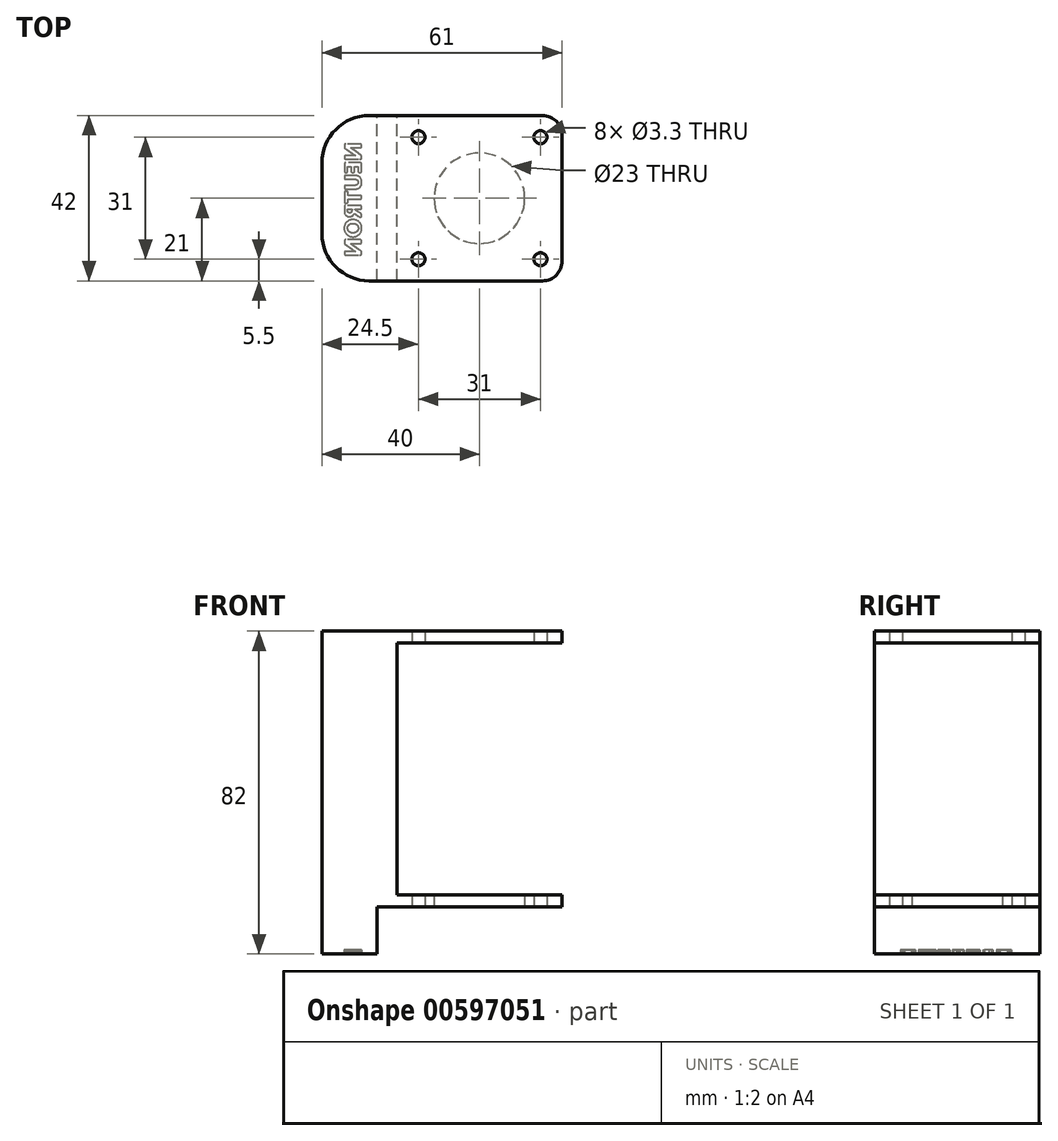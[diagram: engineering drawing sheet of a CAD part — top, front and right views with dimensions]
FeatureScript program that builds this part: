
annotation { "Feature Type Name" : "Feature", "Feature Type Description" : "" }
export const myFeature = defineFeature(function(context is Context, id is Id, definition is map)
    precondition{}
    {
        {
            var Q0;
            Q0=qCreatedBy(makeId("Top.planeOp"),FACE);
            var sketch = newSketch(context, id + "F0", { "sketchPlane" : qUnion([Q0])});
            skLineSegment(sketch, "E0.bottom", {"start": v(21, -21) * mm, "end": v(-21, -21) * mm});
            skLineSegment(sketch, "E0.top", {"start": v(21, 21) * mm, "end": v(-21, 21) * mm});
            skLineSegment(sketch, "E0.left", {"start": v(21, -21) * mm, "end": v(21, 21) * mm});
            skLineSegment(sketch, "E0.right", {"start": v(-21, -21) * mm, "end": v(-21, 21) * mm});
            skPoint(sketch, "E0.middle", {"position": v(0, 0) * mm});
            skSolve(sketch);
        }
        {
            var Q0;
            Q0=makeQuery(id+"F0.imprint","IMPRINT",FACE,{"disambiguationData":[TD([[makeQuery(id+"F0.imprint","IMPRINT",EDGE,{"derivedFrom":sQuery(id+"F0.wireOp",EDGE,"E0.bottom")}),-1.0]])]});
            extrude(context, id + "F1", {"entities" : qUnion([Q0]), "depth" : 3 * mm});
        }
        {
            var Q0;
            Q0=makeQuery(id+"F1.opExtrude","CAP_FACE",FACE,{"disambiguationData":[OSD([sQuery(id+"F0.wireOp",EDGE,"E0.bottom"),sQuery(id+"F0.wireOp",EDGE,"E0.top"),sQuery(id+"F0.wireOp",EDGE,"E0.left"),sQuery(id+"F0.wireOp",EDGE,"E0.right")])],"isStart":true});
            var sketch = newSketch(context, id + "F2", { "sketchPlane" : qUnion([Q0])});
            skLineSegment(sketch, "E1.bottom", {"start": v(-15.5, 15.5) * mm, "end": v(15.5, 15.5) * mm});
            skLineSegment(sketch, "E1.top", {"start": v(-15.5, -15.5) * mm, "end": v(15.5, -15.5) * mm});
            skLineSegment(sketch, "E1.left", {"start": v(-15.5, 15.5) * mm, "end": v(-15.5, -15.5) * mm});
            skLineSegment(sketch, "E1.right", {"start": v(15.5, 15.5) * mm, "end": v(15.5, -15.5) * mm});
            skPoint(sketch, "E1.middle", {"position": v(0, 0) * mm});
            skCircle(sketch, "E2", {"center": v(0, 0) * mm, "radius": 11.5 * mm});
            skSolve(sketch);
        }
        {
            var Q0;
            Q0=makeQuery(id+"F2.imprint","IMPRINT",FACE,{"disambiguationData":[TD([[makeQuery(id+"F2.imprint","IMPRINT",EDGE,{"derivedFrom":sQuery(id+"F2.wireOp",EDGE,"E2")}),1.0]])]});
            extrude(context, id + "F3", {"entities" : qUnion([Q0]), "operationType" : NewBodyOperationType.REMOVE, "oppositeDirection" : true, "depth" : 25 * mm});
        }
        {
            var Q0;
            Q0=makeQuery(id+"F1.opExtrude","SWEPT_FACE",FACE,{"disambiguationData":[OSD([sQuery(id+"F0.wireOp",EDGE,"E0.right")])]});
            var sketch = newSketch(context, id + "F4", { "sketchPlane" : qUnion([Q0])});
            skLineSegment(sketch, "E3.bottom", {"start": v(21, 0) * mm, "end": v(-21, 0) * mm});
            skLineSegment(sketch, "E3.top", {"start": v(21, 70) * mm, "end": v(-21, 70) * mm});
            skLineSegment(sketch, "E3.left", {"start": v(21, 0) * mm, "end": v(21, 70) * mm});
            skLineSegment(sketch, "E3.right", {"start": v(-21, 0) * mm, "end": v(-21, 70) * mm});
            skSolve(sketch);
        }
        {
            var Q0;
            {var subQ0=sQuery(id+"F4.wireOp",EDGE,"E3.bottom");Q0=makeQuery(id+"F4.imprint","IMPRINT",FACE,{"disambiguationData":[TD([[makeQuery(id+"F4.imprint","IMPRINT",EDGE,{"derivedFrom":subQ0}),-1.0]])]});}
            var Q1;
            {var subQ0=sQuery(id+"F4.wireOp",EDGE,"E3.top");Q1=makeQuery(id+"F4.imprint","IMPRINT",FACE,{"disambiguationData":[TD([[makeQuery(id+"F4.imprint","IMPRINT",EDGE,{"derivedFrom":subQ0}),1.0]])]});}
            extrude(context, id + "F5", {"entities" : qUnion([Q0, Q1]), "operationType" : NewBodyOperationType.ADD, "depth" : 19 * mm});
        }
        {
            var Q0;
            Q0=makeQuery(id+"F5.opExtrude","CAP_FACE",FACE,{"disambiguationData":[OSD([sQuery(id+"F4.wireOp",EDGE,"E3.bottom"),sQuery(id+"F4.wireOp",EDGE,"E3.top"),sQuery(id+"F4.wireOp",EDGE,"E3.left"),sQuery(id+"F4.wireOp",EDGE,"E3.right")])],"isStart":true});
            var sketch = newSketch(context, id + "F6", { "sketchPlane" : qUnion([Q0])});
            skLineSegment(sketch, "E4.bottom", {"start": v(21, 70) * mm, "end": v(-21, 70) * mm});
            skLineSegment(sketch, "E4.top", {"start": v(21, 67) * mm, "end": v(-21, 67) * mm});
            skLineSegment(sketch, "E4.left", {"start": v(21, 70) * mm, "end": v(21, 67) * mm});
            skLineSegment(sketch, "E4.right", {"start": v(-21, 70) * mm, "end": v(-21, 67) * mm});
            skSolve(sketch);
        }
        {
            var Q0;
            Q0=qSketchRegion(id+"F6",true);
            extrude(context, id + "F7", {"entities" : qUnion([Q0]), "operationType" : NewBodyOperationType.ADD, "depth" : 42 * mm});
        }
        {
            var Q0;
            Q0=makeQuery(id+"F1.opExtrude","SWEPT_EDGE",EDGE,{"disambiguationData":[OSD([sQuery(id+"F0.wireOp",EDGE,"E0.top"),sQuery(id+"F0.wireOp",EDGE,"E0.left")])]});
            var Q1;
            Q1=makeQuery(id+"F1.opExtrude","SWEPT_EDGE",EDGE,{"disambiguationData":[OSD([sQuery(id+"F0.wireOp",EDGE,"E0.bottom"),sQuery(id+"F0.wireOp",EDGE,"E0.left")])]});
            var Q2;
            Q2=makeQuery(id+"F7.opExtrude","CAP_EDGE",EDGE,{"disambiguationData":[OSD([sQuery(id+"F6.wireOp",EDGE,"E4.right")])],"isStart":false});
            var Q3;
            Q3=makeQuery(id+"F7.opExtrude","CAP_EDGE",EDGE,{"disambiguationData":[OSD([sQuery(id+"F6.wireOp",EDGE,"E4.left")])],"isStart":false});
            fillet(context, id + "F8", {"entities" : qUnion([Q0, Q1, Q2, Q3]), "radius" : 5 * mm, "tangentPropagation" : true, "allowEdgeOverflow" : false});
        }
        {
            var Q0;
            Q0=sQuery(id+"F2.wireOp",VERTEX,"E1.left.end");
            var Q1;
            Q1=sQuery(id+"F2.wireOp",VERTEX,"E1.right.end");
            var Q2;
            Q2=sQuery(id+"F2.wireOp",VERTEX,"E1.right.start");
            var Q3;
            Q3=sQuery(id+"F2.wireOp",VERTEX,"E1.left.start");
            var Q4;
            Q4=makeQuery(id+"F1.opExtrude","SWEPT_BODY",BODY,{"disambiguationData":[OSD([sQuery(id+"F0.wireOp",EDGE,"E0.bottom"),sQuery(id+"F0.wireOp",EDGE,"E0.top"),sQuery(id+"F0.wireOp",EDGE,"E0.left"),sQuery(id+"F0.wireOp",EDGE,"E0.right")])]});
            hole(context, id + "F9", {"style" : HoleStyle.SIMPLE, "endStyle" : HoleEndStyle.THROUGH, "standardTappedOrClearance" : lookupTablePath({ "standard" : "ISO", "fit" : "Normal", "size" : "M3", "type" : "Clearance" }), "standardBlindInLast" : lookupTablePath({ "fit" : "Standard", "standard" : "ISO", "size" : "M3", "type" : "Clearance" }), "holeDiameter" : 3.3 * mm, "tappedDepth" : 12 * mm, "tapClearance" : 3, "locations" : qUnion([Q0, Q1, Q2, Q3]), "scope" : qUnion([Q4])});
        }
        {
            var Q0;
            Q0=makeQuery(id+"F5.opExtrude","CAP_EDGE",EDGE,{"disambiguationData":[OSD([sQuery(id+"F4.wireOp",EDGE,"E3.left")])],"isStart":false});
            var Q1;
            Q1=makeQuery(id+"F5.opExtrude","CAP_EDGE",EDGE,{"disambiguationData":[OSD([sQuery(id+"F4.wireOp",EDGE,"E3.right")])],"isStart":false});
            fillet(context, id + "F10", {"entities" : qUnion([Q0, Q1]), "radius" : 12 * mm, "tangentPropagation" : true, "allowEdgeOverflow" : false});
        }
        {
            var Q0;
            Q0=makeQuery(id+"F5.boolean.opBoolean","MERGE",FACE,{"derivedFrom":[makeQuery(id+"F1.opExtrude","CAP_FACE",FACE,{"disambiguationData":[OSD([sQuery(id+"F0.wireOp",EDGE,"E0.bottom"),sQuery(id+"F0.wireOp",EDGE,"E0.top"),sQuery(id+"F0.wireOp",EDGE,"E0.left"),sQuery(id+"F0.wireOp",EDGE,"E0.right")])],"isStart":true}),makeQuery(id+"F5.opExtrude","SWEPT_FACE",FACE,{"disambiguationData":[OSD([sQuery(id+"F4.wireOp",EDGE,"E3.bottom")])]})]});
            var sketch = newSketch(context, id + "F11", { "sketchPlane" : qUnion([Q0])});
            skLineSegment(sketch, "E5", {"start": v(-26, 21) * mm, "end": v(-26, -21) * mm});
            skSolve(sketch);
        }
        {
            var Q0;
            Q0=qSketchRegion(id+"F11",true);
            var Q1;
            Q1=makeQuery(id+"F11.imprint","IMPRINT",FACE,{"disambiguationData":[TD([[makeQuery(id+"F11.imprint","IMPRINT",EDGE,{"derivedFrom":sQuery(id+"F11.wireOp",EDGE,"xwHfM6YB-dKn8-eSAS-4Oin-q8f2QlFwRjm7")}),1.0]])]});
            var Q2;
            {var subQ6=sQuery(id+"F11.wireOp",EDGE,"E5");Q2=makeQuery(id+"F11.imprint","IMPRINT",FACE,{"disambiguationData":[TD([[makeQuery(id+"F11.imprint","IMPRINT",EDGE,{"derivedFrom":subQ6}),-1.0]])]});}
            extrude(context, id + "F12", {"entities" : qUnion([Q0, Q1, Q2]), "operationType" : NewBodyOperationType.ADD, "depth" : 12 * mm});
        }
        {
            var Q0;
            Q0=makeQuery(id+"F12.opExtrude","CAP_FACE",FACE,{"disambiguationData":[OSD([sQuery(id+"F0.wireOp",EDGE,"E0.bottom"),sQuery(id+"F0.wireOp",EDGE,"E0.top"),sQuery(id+"F0.wireOp",EDGE,"E0.left"),sQuery(id+"F0.wireOp",EDGE,"E0.right"),sQuery(id+"F4.wireOp",EDGE,"E3.bottom"),sQuery(id+"F4.wireOp",EDGE,"E3.left"),sQuery(id+"F4.wireOp",EDGE,"E3.right"),sQuery(id+"F11.wireOp",EDGE,"xwHfM6YB-dKn8-eSAS-4Oin-q8f2QlFwRjm7")])],"isStart":false});
            var sketch = newSketch(context, id + "F13", { "sketchPlane" : qUnion([Q0])});
            skLineSegment(sketch, "E6", {"start": v(-34.33, -10.53) * mm, "end": v(-34.33, -10.5) * mm});
            skLineSegment(sketch, "E7", {"start": v(-34.33, -10.5) * mm, "end": v(-34.33, -10.44) * mm});
            skLineSegment(sketch, "E8", {"start": v(-34.33, -10.44) * mm, "end": v(-34.33, -10.36) * mm});
            skLineSegment(sketch, "E9", {"start": v(-34.33, -10.36) * mm, "end": v(-34.33, -10.28) * mm});
            skLineSegment(sketch, "E10", {"start": v(-34.33, -10.28) * mm, "end": v(-34.33, -10.23) * mm});
            skLineSegment(sketch, "E11", {"start": v(-34.33, -10.23) * mm, "end": v(-34.33, -10.18) * mm});
            skLineSegment(sketch, "E12", {"start": v(-34.33, -10.18) * mm, "end": v(-34.3, -10.1) * mm});
            skLineSegment(sketch, "E13", {"start": v(-34.3, -10.1) * mm, "end": v(-34.26, -10.02) * mm});
            skLineSegment(sketch, "E14", {"start": v(-34.26, -10.02) * mm, "end": v(-34.2, -9.97) * mm});
            skLineSegment(sketch, "E15", {"start": v(-34.2, -9.97) * mm, "end": v(-34.12, -9.93) * mm});
            skLineSegment(sketch, "E16", {"start": v(-34.12, -9.93) * mm, "end": v(-34.03, -9.91) * mm});
            skLineSegment(sketch, "E17", {"start": v(-34.03, -9.91) * mm, "end": v(-33.76, -9.91) * mm});
            skLineSegment(sketch, "E18", {"start": v(-33.76, -9.91) * mm, "end": v(-33.01, -9.91) * mm});
            skLineSegment(sketch, "E19", {"start": v(-33.01, -9.91) * mm, "end": v(-32.03, -9.91) * mm});
            skLineSegment(sketch, "E20", {"start": v(-32.03, -9.91) * mm, "end": v(-31.07, -9.91) * mm});
            skLineSegment(sketch, "E21", {"start": v(-31.07, -9.91) * mm, "end": v(-30.41, -9.91) * mm});
            skLineSegment(sketch, "E22", {"start": v(-30.41, -9.91) * mm, "end": v(-30.23, -9.91) * mm});
            skLineSegment(sketch, "E23", {"start": v(-30.23, -9.91) * mm, "end": v(-30.15, -9.93) * mm});
            skLineSegment(sketch, "E24", {"start": v(-30.15, -9.93) * mm, "end": v(-30.07, -9.98) * mm});
            skLineSegment(sketch, "E25", {"start": v(-30.07, -9.98) * mm, "end": v(-30.01, -10.04) * mm});
            skLineSegment(sketch, "E26", {"start": v(-30.01, -10.04) * mm, "end": v(-29.97, -10.11) * mm});
            skLineSegment(sketch, "E27", {"start": v(-29.97, -10.11) * mm, "end": v(-29.95, -10.2) * mm});
            skLineSegment(sketch, "E28", {"start": v(-29.95, -10.2) * mm, "end": v(-29.95, -10.25) * mm});
            skLineSegment(sketch, "E29", {"start": v(-29.95, -10.25) * mm, "end": v(-29.95, -10.33) * mm});
            skLineSegment(sketch, "E30", {"start": v(-29.95, -10.33) * mm, "end": v(-29.95, -10.45) * mm});
            skLineSegment(sketch, "E31", {"start": v(-29.95, -10.45) * mm, "end": v(-29.95, -10.56) * mm});
            skLineSegment(sketch, "E32", {"start": v(-29.95, -10.56) * mm, "end": v(-29.95, -10.65) * mm});
            skLineSegment(sketch, "E33", {"start": v(-29.95, -10.65) * mm, "end": v(-29.95, -10.68) * mm});
            skLineSegment(sketch, "E34", {"start": v(-29.95, -10.68) * mm, "end": v(-29.96, -10.74) * mm});
            skLineSegment(sketch, "E35", {"start": v(-29.96, -10.74) * mm, "end": v(-29.98, -10.79) * mm});
            skLineSegment(sketch, "E36", {"start": v(-29.98, -10.79) * mm, "end": v(-30, -10.83) * mm});
            skLineSegment(sketch, "E37", {"start": v(-30, -10.83) * mm, "end": v(-30.03, -10.88) * mm});
            skLineSegment(sketch, "E38", {"start": v(-30.03, -10.88) * mm, "end": v(-30.07, -10.91) * mm});
            skLineSegment(sketch, "E39", {"start": v(-30.07, -10.91) * mm, "end": v(-30.2, -11) * mm});
            skLineSegment(sketch, "E40", {"start": v(-30.2, -11) * mm, "end": v(-30.67, -11.34) * mm});
            skLineSegment(sketch, "E41", {"start": v(-30.67, -11.34) * mm, "end": v(-31.35, -11.82) * mm});
            skLineSegment(sketch, "E42", {"start": v(-31.35, -11.82) * mm, "end": v(-32.06, -12.32) * mm});
            skLineSegment(sketch, "E43", {"start": v(-32.06, -12.32) * mm, "end": v(-32.6, -12.7) * mm});
            skLineSegment(sketch, "E44", {"start": v(-32.6, -12.7) * mm, "end": v(-32.78, -12.83) * mm});
            skLineSegment(sketch, "E45", {"start": v(-32.78, -12.83) * mm, "end": v(-32.52, -12.83) * mm});
            skLineSegment(sketch, "E46", {"start": v(-32.52, -12.83) * mm, "end": v(-31.97, -12.83) * mm});
            skLineSegment(sketch, "E47", {"start": v(-31.97, -12.83) * mm, "end": v(-31.3, -12.83) * mm});
            skLineSegment(sketch, "E48", {"start": v(-31.3, -12.83) * mm, "end": v(-30.68, -12.83) * mm});
            skLineSegment(sketch, "E49", {"start": v(-30.68, -12.83) * mm, "end": v(-30.3, -12.83) * mm});
            skLineSegment(sketch, "E50", {"start": v(-30.3, -12.83) * mm, "end": v(-30.21, -12.84) * mm});
            skLineSegment(sketch, "E51", {"start": v(-30.21, -12.84) * mm, "end": v(-30.13, -12.86) * mm});
            skLineSegment(sketch, "E52", {"start": v(-30.13, -12.86) * mm, "end": v(-30.06, -12.9) * mm});
            skLineSegment(sketch, "E53", {"start": v(-30.06, -12.9) * mm, "end": v(-30, -12.97) * mm});
            skLineSegment(sketch, "E54", {"start": v(-30, -12.97) * mm, "end": v(-29.97, -13.05) * mm});
            skLineSegment(sketch, "E55", {"start": v(-29.97, -13.05) * mm, "end": v(-29.95, -13.14) * mm});
            skLineSegment(sketch, "E56", {"start": v(-29.95, -13.14) * mm, "end": v(-29.95, -13.17) * mm});
            skLineSegment(sketch, "E57", {"start": v(-29.95, -13.17) * mm, "end": v(-29.95, -13.24) * mm});
            skLineSegment(sketch, "E58", {"start": v(-29.95, -13.24) * mm, "end": v(-29.95, -13.32) * mm});
            skLineSegment(sketch, "E59", {"start": v(-29.95, -13.32) * mm, "end": v(-29.95, -13.4) * mm});
            skLineSegment(sketch, "E60", {"start": v(-29.95, -13.4) * mm, "end": v(-29.95, -13.46) * mm});
            skLineSegment(sketch, "E61", {"start": v(-29.95, -13.46) * mm, "end": v(-29.96, -13.5) * mm});
            skLineSegment(sketch, "E62", {"start": v(-29.96, -13.5) * mm, "end": v(-29.98, -13.6) * mm});
            skLineSegment(sketch, "E63", {"start": v(-29.98, -13.6) * mm, "end": v(-30.02, -13.66) * mm});
            skLineSegment(sketch, "E64", {"start": v(-30.02, -13.66) * mm, "end": v(-30.09, -13.72) * mm});
            skLineSegment(sketch, "E65", {"start": v(-30.09, -13.72) * mm, "end": v(-30.16, -13.76) * mm});
            skLineSegment(sketch, "E66", {"start": v(-30.16, -13.76) * mm, "end": v(-30.25, -13.78) * mm});
            skLineSegment(sketch, "E67", {"start": v(-30.25, -13.78) * mm, "end": v(-30.52, -13.78) * mm});
            skLineSegment(sketch, "E68", {"start": v(-30.52, -13.78) * mm, "end": v(-31.27, -13.78) * mm});
            skLineSegment(sketch, "E69", {"start": v(-31.27, -13.78) * mm, "end": v(-32.25, -13.78) * mm});
            skLineSegment(sketch, "E70", {"start": v(-32.25, -13.78) * mm, "end": v(-33.2, -13.78) * mm});
            skLineSegment(sketch, "E71", {"start": v(-33.2, -13.78) * mm, "end": v(-33.87, -13.78) * mm});
            skLineSegment(sketch, "E72", {"start": v(-33.87, -13.78) * mm, "end": v(-34.05, -13.77) * mm});
            skLineSegment(sketch, "E73", {"start": v(-34.05, -13.77) * mm, "end": v(-34.14, -13.75) * mm});
            skLineSegment(sketch, "E74", {"start": v(-34.14, -13.75) * mm, "end": v(-34.21, -13.71) * mm});
            skLineSegment(sketch, "E75", {"start": v(-34.21, -13.71) * mm, "end": v(-34.27, -13.65) * mm});
            skLineSegment(sketch, "E76", {"start": v(-34.27, -13.65) * mm, "end": v(-34.31, -13.57) * mm});
            skLineSegment(sketch, "E77", {"start": v(-34.31, -13.57) * mm, "end": v(-34.33, -13.49) * mm});
            skLineSegment(sketch, "E78", {"start": v(-34.33, -13.49) * mm, "end": v(-34.33, -13.44) * mm});
            skLineSegment(sketch, "E79", {"start": v(-34.33, -13.44) * mm, "end": v(-34.33, -13.35) * mm});
            skLineSegment(sketch, "E80", {"start": v(-34.33, -13.35) * mm, "end": v(-34.33, -13.23) * mm});
            skLineSegment(sketch, "E81", {"start": v(-34.33, -13.23) * mm, "end": v(-34.33, -13.11) * mm});
            skLineSegment(sketch, "E82", {"start": v(-34.33, -13.11) * mm, "end": v(-34.33, -13.03) * mm});
            skLineSegment(sketch, "E83", {"start": v(-34.33, -13.03) * mm, "end": v(-34.33, -12.99) * mm});
            skLineSegment(sketch, "E84", {"start": v(-34.33, -12.99) * mm, "end": v(-34.32, -12.94) * mm});
            skLineSegment(sketch, "E85", {"start": v(-34.32, -12.94) * mm, "end": v(-34.3, -12.89) * mm});
            skLineSegment(sketch, "E86", {"start": v(-34.3, -12.89) * mm, "end": v(-34.28, -12.84) * mm});
            skLineSegment(sketch, "E87", {"start": v(-34.28, -12.84) * mm, "end": v(-34.25, -12.8) * mm});
            skLineSegment(sketch, "E88", {"start": v(-34.25, -12.8) * mm, "end": v(-34.21, -12.76) * mm});
            skLineSegment(sketch, "E89", {"start": v(-34.21, -12.76) * mm, "end": v(-34.1, -12.67) * mm});
            skLineSegment(sketch, "E90", {"start": v(-34.1, -12.67) * mm, "end": v(-33.62, -12.34) * mm});
            skLineSegment(sketch, "E91", {"start": v(-33.62, -12.34) * mm, "end": v(-32.94, -11.85) * mm});
            skLineSegment(sketch, "E92", {"start": v(-32.94, -11.85) * mm, "end": v(-32.24, -11.35) * mm});
            skLineSegment(sketch, "E93", {"start": v(-32.24, -11.35) * mm, "end": v(-31.7, -10.97) * mm});
            skLineSegment(sketch, "E94", {"start": v(-31.7, -10.97) * mm, "end": v(-31.52, -10.84) * mm});
            skLineSegment(sketch, "E95", {"start": v(-31.52, -10.84) * mm, "end": v(-31.78, -10.84) * mm});
            skLineSegment(sketch, "E96", {"start": v(-31.78, -10.84) * mm, "end": v(-32.33, -10.84) * mm});
            skLineSegment(sketch, "E97", {"start": v(-32.33, -10.84) * mm, "end": v(-33, -10.84) * mm});
            skLineSegment(sketch, "E98", {"start": v(-33, -10.84) * mm, "end": v(-33.6, -10.84) * mm});
            skLineSegment(sketch, "E99", {"start": v(-33.6, -10.84) * mm, "end": v(-33.97, -10.84) * mm});
            skLineSegment(sketch, "E100", {"start": v(-33.97, -10.84) * mm, "end": v(-34.07, -10.83) * mm});
            skLineSegment(sketch, "E101", {"start": v(-34.07, -10.83) * mm, "end": v(-34.15, -10.8) * mm});
            skLineSegment(sketch, "E102", {"start": v(-34.15, -10.8) * mm, "end": v(-34.22, -10.76) * mm});
            skLineSegment(sketch, "E103", {"start": v(-34.22, -10.76) * mm, "end": v(-34.28, -10.7) * mm});
            skLineSegment(sketch, "E104", {"start": v(-34.28, -10.7) * mm, "end": v(-34.32, -10.62) * mm});
            skLineSegment(sketch, "E105", {"start": v(-34.32, -10.62) * mm, "end": v(-34.33, -10.53) * mm});
            skLineSegment(sketch, "E106", {"start": v(-34.33, -8.72) * mm, "end": v(-34.33, -8.52) * mm});
            skLineSegment(sketch, "E107", {"start": v(-34.33, -8.52) * mm, "end": v(-34.33, -8.07) * mm});
            skLineSegment(sketch, "E108", {"start": v(-34.33, -8.07) * mm, "end": v(-34.33, -7.52) * mm});
            skLineSegment(sketch, "E109", {"start": v(-34.33, -7.52) * mm, "end": v(-34.33, -7.06) * mm});
            skLineSegment(sketch, "E110", {"start": v(-34.33, -7.06) * mm, "end": v(-34.33, -6.87) * mm});
            skLineSegment(sketch, "E111", {"start": v(-34.33, -6.87) * mm, "end": v(-34.31, -6.77) * mm});
            skLineSegment(sketch, "E112", {"start": v(-34.31, -6.77) * mm, "end": v(-34.27, -6.69) * mm});
            skLineSegment(sketch, "E113", {"start": v(-34.27, -6.69) * mm, "end": v(-34.2, -6.62) * mm});
            skLineSegment(sketch, "E114", {"start": v(-34.2, -6.62) * mm, "end": v(-34.12, -6.58) * mm});
            skLineSegment(sketch, "E115", {"start": v(-34.12, -6.58) * mm, "end": v(-34.02, -6.56) * mm});
            skLineSegment(sketch, "E116", {"start": v(-34.02, -6.56) * mm, "end": v(-34, -6.56) * mm});
            skLineSegment(sketch, "E117", {"start": v(-34, -6.56) * mm, "end": v(-33.93, -6.56) * mm});
            skLineSegment(sketch, "E118", {"start": v(-33.93, -6.56) * mm, "end": v(-33.86, -6.56) * mm});
            skLineSegment(sketch, "E119", {"start": v(-33.86, -6.56) * mm, "end": v(-33.8, -6.56) * mm});
            skLineSegment(sketch, "E120", {"start": v(-33.8, -6.56) * mm, "end": v(-33.77, -6.56) * mm});
            skLineSegment(sketch, "E121", {"start": v(-33.77, -6.56) * mm, "end": v(-33.67, -6.58) * mm});
            skLineSegment(sketch, "E122", {"start": v(-33.67, -6.58) * mm, "end": v(-33.59, -6.62) * mm});
            skLineSegment(sketch, "E123", {"start": v(-33.59, -6.62) * mm, "end": v(-33.52, -6.69) * mm});
            skLineSegment(sketch, "E124", {"start": v(-33.52, -6.69) * mm, "end": v(-33.48, -6.77) * mm});
            skLineSegment(sketch, "E125", {"start": v(-33.48, -6.77) * mm, "end": v(-33.46, -6.87) * mm});
            skLineSegment(sketch, "E126", {"start": v(-33.46, -6.87) * mm, "end": v(-33.46, -7) * mm});
            skLineSegment(sketch, "E127", {"start": v(-33.46, -7) * mm, "end": v(-33.46, -7.3) * mm});
            skLineSegment(sketch, "E128", {"start": v(-33.46, -7.3) * mm, "end": v(-33.46, -7.66) * mm});
            skLineSegment(sketch, "E129", {"start": v(-33.46, -7.66) * mm, "end": v(-33.46, -7.96) * mm});
            skLineSegment(sketch, "E130", {"start": v(-33.46, -7.96) * mm, "end": v(-33.46, -8.08) * mm});
            skLineSegment(sketch, "E131", {"start": v(-33.46, -8.08) * mm, "end": v(-33.37, -8.08) * mm});
            skLineSegment(sketch, "E132", {"start": v(-33.37, -8.08) * mm, "end": v(-33.15, -8.08) * mm});
            skLineSegment(sketch, "E133", {"start": v(-33.15, -8.08) * mm, "end": v(-32.9, -8.08) * mm});
            skLineSegment(sketch, "E134", {"start": v(-32.9, -8.08) * mm, "end": v(-32.67, -8.08) * mm});
            skLineSegment(sketch, "E135", {"start": v(-32.67, -8.08) * mm, "end": v(-32.58, -8.08) * mm});
            skLineSegment(sketch, "E136", {"start": v(-32.58, -8.08) * mm, "end": v(-32.58, -7.96) * mm});
            skLineSegment(sketch, "E137", {"start": v(-32.58, -7.96) * mm, "end": v(-32.58, -7.66) * mm});
            skLineSegment(sketch, "E138", {"start": v(-32.58, -7.66) * mm, "end": v(-32.58, -7.3) * mm});
            skLineSegment(sketch, "E139", {"start": v(-32.58, -7.3) * mm, "end": v(-32.58, -7) * mm});
            skLineSegment(sketch, "E140", {"start": v(-32.58, -7) * mm, "end": v(-32.58, -6.87) * mm});
            skLineSegment(sketch, "E141", {"start": v(-32.58, -6.87) * mm, "end": v(-32.56, -6.77) * mm});
            skLineSegment(sketch, "E142", {"start": v(-32.56, -6.77) * mm, "end": v(-32.52, -6.69) * mm});
            skLineSegment(sketch, "E143", {"start": v(-32.52, -6.69) * mm, "end": v(-32.45, -6.62) * mm});
            skLineSegment(sketch, "E144", {"start": v(-32.45, -6.62) * mm, "end": v(-32.37, -6.58) * mm});
            skLineSegment(sketch, "E145", {"start": v(-32.37, -6.58) * mm, "end": v(-32.27, -6.56) * mm});
            skLineSegment(sketch, "E146", {"start": v(-32.27, -6.56) * mm, "end": v(-32.25, -6.56) * mm});
            skLineSegment(sketch, "E147", {"start": v(-32.25, -6.56) * mm, "end": v(-32.19, -6.56) * mm});
            skLineSegment(sketch, "E148", {"start": v(-32.19, -6.56) * mm, "end": v(-32.12, -6.56) * mm});
            skLineSegment(sketch, "E149", {"start": v(-32.12, -6.56) * mm, "end": v(-32.06, -6.56) * mm});
            skLineSegment(sketch, "E150", {"start": v(-32.06, -6.56) * mm, "end": v(-32.04, -6.56) * mm});
            skLineSegment(sketch, "E151", {"start": v(-32.04, -6.56) * mm, "end": v(-31.94, -6.58) * mm});
            skLineSegment(sketch, "E152", {"start": v(-31.94, -6.58) * mm, "end": v(-31.85, -6.62) * mm});
            skLineSegment(sketch, "E153", {"start": v(-31.85, -6.62) * mm, "end": v(-31.79, -6.69) * mm});
            skLineSegment(sketch, "E154", {"start": v(-31.79, -6.69) * mm, "end": v(-31.74, -6.77) * mm});
            skLineSegment(sketch, "E155", {"start": v(-31.74, -6.77) * mm, "end": v(-31.73, -6.87) * mm});
            skLineSegment(sketch, "E156", {"start": v(-31.73, -6.87) * mm, "end": v(-31.73, -7) * mm});
            skLineSegment(sketch, "E157", {"start": v(-31.73, -7) * mm, "end": v(-31.73, -7.3) * mm});
            skLineSegment(sketch, "E158", {"start": v(-31.73, -7.3) * mm, "end": v(-31.73, -7.66) * mm});
            skLineSegment(sketch, "E159", {"start": v(-31.73, -7.66) * mm, "end": v(-31.73, -7.96) * mm});
            skLineSegment(sketch, "E160", {"start": v(-31.73, -7.96) * mm, "end": v(-31.73, -8.08) * mm});
            skLineSegment(sketch, "E161", {"start": v(-31.73, -8.08) * mm, "end": v(-31.63, -8.08) * mm});
            skLineSegment(sketch, "E162", {"start": v(-31.63, -8.08) * mm, "end": v(-31.4, -8.08) * mm});
            skLineSegment(sketch, "E163", {"start": v(-31.4, -8.08) * mm, "end": v(-31.14, -8.08) * mm});
            skLineSegment(sketch, "E164", {"start": v(-31.14, -8.08) * mm, "end": v(-30.91, -8.08) * mm});
            skLineSegment(sketch, "E165", {"start": v(-30.91, -8.08) * mm, "end": v(-30.82, -8.08) * mm});
            skLineSegment(sketch, "E166", {"start": v(-30.82, -8.08) * mm, "end": v(-30.82, -7.96) * mm});
            skLineSegment(sketch, "E167", {"start": v(-30.82, -7.96) * mm, "end": v(-30.82, -7.66) * mm});
            skLineSegment(sketch, "E168", {"start": v(-30.82, -7.66) * mm, "end": v(-30.82, -7.3) * mm});
            skLineSegment(sketch, "E169", {"start": v(-30.82, -7.3) * mm, "end": v(-30.82, -7) * mm});
            skLineSegment(sketch, "E170", {"start": v(-30.82, -7) * mm, "end": v(-30.82, -6.87) * mm});
            skLineSegment(sketch, "E171", {"start": v(-30.82, -6.87) * mm, "end": v(-30.8, -6.77) * mm});
            skLineSegment(sketch, "E172", {"start": v(-30.8, -6.77) * mm, "end": v(-30.76, -6.69) * mm});
            skLineSegment(sketch, "E173", {"start": v(-30.76, -6.69) * mm, "end": v(-30.7, -6.62) * mm});
            skLineSegment(sketch, "E174", {"start": v(-30.7, -6.62) * mm, "end": v(-30.6, -6.58) * mm});
            skLineSegment(sketch, "E175", {"start": v(-30.6, -6.58) * mm, "end": v(-30.51, -6.56) * mm});
            skLineSegment(sketch, "E176", {"start": v(-30.51, -6.56) * mm, "end": v(-30.48, -6.56) * mm});
            skLineSegment(sketch, "E177", {"start": v(-30.48, -6.56) * mm, "end": v(-30.42, -6.56) * mm});
            skLineSegment(sketch, "E178", {"start": v(-30.42, -6.56) * mm, "end": v(-30.35, -6.56) * mm});
            skLineSegment(sketch, "E179", {"start": v(-30.35, -6.56) * mm, "end": v(-30.29, -6.56) * mm});
            skLineSegment(sketch, "E180", {"start": v(-30.29, -6.56) * mm, "end": v(-30.26, -6.56) * mm});
            skLineSegment(sketch, "E181", {"start": v(-30.26, -6.56) * mm, "end": v(-30.16, -6.58) * mm});
            skLineSegment(sketch, "E182", {"start": v(-30.16, -6.58) * mm, "end": v(-30.08, -6.62) * mm});
            skLineSegment(sketch, "E183", {"start": v(-30.08, -6.62) * mm, "end": v(-30.01, -6.69) * mm});
            skLineSegment(sketch, "E184", {"start": v(-30.01, -6.69) * mm, "end": v(-29.97, -6.77) * mm});
            skLineSegment(sketch, "E185", {"start": v(-29.97, -6.77) * mm, "end": v(-29.95, -6.87) * mm});
            skLineSegment(sketch, "E186", {"start": v(-29.95, -6.87) * mm, "end": v(-29.95, -7.06) * mm});
            skLineSegment(sketch, "E187", {"start": v(-29.95, -7.06) * mm, "end": v(-29.95, -7.52) * mm});
            skLineSegment(sketch, "E188", {"start": v(-29.95, -7.52) * mm, "end": v(-29.95, -8.07) * mm});
            skLineSegment(sketch, "E189", {"start": v(-29.95, -8.07) * mm, "end": v(-29.95, -8.52) * mm});
            skLineSegment(sketch, "E190", {"start": v(-29.95, -8.52) * mm, "end": v(-29.95, -8.72) * mm});
            skLineSegment(sketch, "E191", {"start": v(-29.95, -8.72) * mm, "end": v(-29.97, -8.81) * mm});
            skLineSegment(sketch, "E192", {"start": v(-29.97, -8.81) * mm, "end": v(-30.01, -8.9) * mm});
            skLineSegment(sketch, "E193", {"start": v(-30.01, -8.9) * mm, "end": v(-30.08, -8.97) * mm});
            skLineSegment(sketch, "E194", {"start": v(-30.08, -8.97) * mm, "end": v(-30.16, -9.01) * mm});
            skLineSegment(sketch, "E195", {"start": v(-30.16, -9.01) * mm, "end": v(-30.26, -9.03) * mm});
            skLineSegment(sketch, "E196", {"start": v(-30.26, -9.03) * mm, "end": v(-30.65, -9.03) * mm});
            skLineSegment(sketch, "E197", {"start": v(-30.65, -9.03) * mm, "end": v(-31.58, -9.03) * mm});
            skLineSegment(sketch, "E198", {"start": v(-31.58, -9.03) * mm, "end": v(-32.7, -9.03) * mm});
            skLineSegment(sketch, "E199", {"start": v(-32.7, -9.03) * mm, "end": v(-33.63, -9.03) * mm});
            skLineSegment(sketch, "E200", {"start": v(-33.63, -9.03) * mm, "end": v(-34.02, -9.03) * mm});
            skLineSegment(sketch, "E201", {"start": v(-34.02, -9.03) * mm, "end": v(-34.12, -9.01) * mm});
            skLineSegment(sketch, "E202", {"start": v(-34.12, -9.01) * mm, "end": v(-34.2, -8.97) * mm});
            skLineSegment(sketch, "E203", {"start": v(-34.2, -8.97) * mm, "end": v(-34.27, -8.9) * mm});
            skLineSegment(sketch, "E204", {"start": v(-34.27, -8.9) * mm, "end": v(-34.31, -8.81) * mm});
            skLineSegment(sketch, "E205", {"start": v(-34.31, -8.81) * mm, "end": v(-34.33, -8.72) * mm});
            skLineSegment(sketch, "E206", {"start": v(-34.33, -5.45) * mm, "end": v(-34.33, -5.42) * mm});
            skLineSegment(sketch, "E207", {"start": v(-34.33, -5.42) * mm, "end": v(-34.33, -5.35) * mm});
            skLineSegment(sketch, "E208", {"start": v(-34.33, -5.35) * mm, "end": v(-34.33, -5.27) * mm});
            skLineSegment(sketch, "E209", {"start": v(-34.33, -5.27) * mm, "end": v(-34.33, -5.19) * mm});
            skLineSegment(sketch, "E210", {"start": v(-34.33, -5.19) * mm, "end": v(-34.33, -5.14) * mm});
            skLineSegment(sketch, "E211", {"start": v(-34.33, -5.14) * mm, "end": v(-34.32, -5.07) * mm});
            skLineSegment(sketch, "E212", {"start": v(-34.32, -5.07) * mm, "end": v(-34.29, -4.99) * mm});
            skLineSegment(sketch, "E213", {"start": v(-34.29, -4.99) * mm, "end": v(-34.23, -4.92) * mm});
            skLineSegment(sketch, "E214", {"start": v(-34.23, -4.92) * mm, "end": v(-34.16, -4.87) * mm});
            skLineSegment(sketch, "E215", {"start": v(-34.16, -4.87) * mm, "end": v(-34.07, -4.84) * mm});
            skLineSegment(sketch, "E216", {"start": v(-34.07, -4.84) * mm, "end": v(-33.97, -4.83) * mm});
            skLineSegment(sketch, "E217", {"start": v(-33.97, -4.83) * mm, "end": v(-33.57, -4.83) * mm});
            skLineSegment(sketch, "E218", {"start": v(-33.57, -4.83) * mm, "end": v(-32.94, -4.83) * mm});
            skLineSegment(sketch, "E219", {"start": v(-32.94, -4.83) * mm, "end": v(-32.29, -4.83) * mm});
            skLineSegment(sketch, "E220", {"start": v(-32.29, -4.83) * mm, "end": v(-31.8, -4.83) * mm});
            skLineSegment(sketch, "E221", {"start": v(-31.8, -4.83) * mm, "end": v(-31.62, -4.83) * mm});
            skLineSegment(sketch, "E222", {"start": v(-31.62, -4.83) * mm, "end": v(-31.49, -4.82) * mm});
            skLineSegment(sketch, "E223", {"start": v(-31.49, -4.82) * mm, "end": v(-31.37, -4.8) * mm});
            skLineSegment(sketch, "E224", {"start": v(-31.37, -4.8) * mm, "end": v(-31.25, -4.76) * mm});
            skLineSegment(sketch, "E225", {"start": v(-31.25, -4.76) * mm, "end": v(-31.15, -4.7) * mm});
            skLineSegment(sketch, "E226", {"start": v(-31.15, -4.7) * mm, "end": v(-31.06, -4.63) * mm});
            skLineSegment(sketch, "E227", {"start": v(-31.06, -4.63) * mm, "end": v(-30.98, -4.55) * mm});
            skLineSegment(sketch, "E228", {"start": v(-30.98, -4.55) * mm, "end": v(-30.92, -4.46) * mm});
            skLineSegment(sketch, "E229", {"start": v(-30.92, -4.46) * mm, "end": v(-30.87, -4.35) * mm});
            skLineSegment(sketch, "E230", {"start": v(-30.87, -4.35) * mm, "end": v(-30.84, -4.24) * mm});
            skLineSegment(sketch, "E231", {"start": v(-30.84, -4.24) * mm, "end": v(-30.83, -4.12) * mm});
            skLineSegment(sketch, "E232", {"start": v(-30.83, -4.12) * mm, "end": v(-30.83, -3.99) * mm});
            skLineSegment(sketch, "E233", {"start": v(-30.83, -3.99) * mm, "end": v(-30.85, -3.85) * mm});
            skLineSegment(sketch, "E234", {"start": v(-30.85, -3.85) * mm, "end": v(-30.89, -3.73) * mm});
            skLineSegment(sketch, "E235", {"start": v(-30.89, -3.73) * mm, "end": v(-30.94, -3.63) * mm});
            skLineSegment(sketch, "E236", {"start": v(-30.94, -3.63) * mm, "end": v(-31, -3.53) * mm});
            skLineSegment(sketch, "E237", {"start": v(-31, -3.53) * mm, "end": v(-31.1, -3.45) * mm});
            skLineSegment(sketch, "E238", {"start": v(-31.1, -3.45) * mm, "end": v(-31.2, -3.38) * mm});
            skLineSegment(sketch, "E239", {"start": v(-31.2, -3.38) * mm, "end": v(-31.3, -3.33) * mm});
            skLineSegment(sketch, "E240", {"start": v(-31.3, -3.33) * mm, "end": v(-31.43, -3.3) * mm});
            skLineSegment(sketch, "E241", {"start": v(-31.43, -3.3) * mm, "end": v(-31.57, -3.28) * mm});
            skLineSegment(sketch, "E242", {"start": v(-31.57, -3.28) * mm, "end": v(-31.7, -3.27) * mm});
            skLineSegment(sketch, "E243", {"start": v(-31.7, -3.27) * mm, "end": v(-31.99, -3.27) * mm});
            skLineSegment(sketch, "E244", {"start": v(-31.99, -3.27) * mm, "end": v(-32.55, -3.27) * mm});
            skLineSegment(sketch, "E245", {"start": v(-32.55, -3.27) * mm, "end": v(-33.2, -3.27) * mm});
            skLineSegment(sketch, "E246", {"start": v(-33.2, -3.27) * mm, "end": v(-33.76, -3.27) * mm});
            skLineSegment(sketch, "E247", {"start": v(-33.76, -3.27) * mm, "end": v(-34.02, -3.27) * mm});
            skLineSegment(sketch, "E248", {"start": v(-34.02, -3.27) * mm, "end": v(-34.1, -3.26) * mm});
            skLineSegment(sketch, "E249", {"start": v(-34.1, -3.26) * mm, "end": v(-34.19, -3.22) * mm});
            skLineSegment(sketch, "E250", {"start": v(-34.19, -3.22) * mm, "end": v(-34.25, -3.16) * mm});
            skLineSegment(sketch, "E251", {"start": v(-34.25, -3.16) * mm, "end": v(-34.3, -3.09) * mm});
            skLineSegment(sketch, "E252", {"start": v(-34.3, -3.09) * mm, "end": v(-34.33, -3) * mm});
            skLineSegment(sketch, "E253", {"start": v(-34.33, -3) * mm, "end": v(-34.33, -2.95) * mm});
            skLineSegment(sketch, "E254", {"start": v(-34.33, -2.95) * mm, "end": v(-34.33, -2.9) * mm});
            skLineSegment(sketch, "E255", {"start": v(-34.33, -2.9) * mm, "end": v(-34.33, -2.8) * mm});
            skLineSegment(sketch, "E256", {"start": v(-34.33, -2.8) * mm, "end": v(-34.33, -2.72) * mm});
            skLineSegment(sketch, "E257", {"start": v(-34.33, -2.72) * mm, "end": v(-34.33, -2.66) * mm});
            skLineSegment(sketch, "E258", {"start": v(-34.33, -2.66) * mm, "end": v(-34.33, -2.62) * mm});
            skLineSegment(sketch, "E259", {"start": v(-34.33, -2.62) * mm, "end": v(-34.3, -2.53) * mm});
            skLineSegment(sketch, "E260", {"start": v(-34.3, -2.53) * mm, "end": v(-34.25, -2.45) * mm});
            skLineSegment(sketch, "E261", {"start": v(-34.25, -2.45) * mm, "end": v(-34.19, -2.4) * mm});
            skLineSegment(sketch, "E262", {"start": v(-34.19, -2.4) * mm, "end": v(-34.1, -2.35) * mm});
            skLineSegment(sketch, "E263", {"start": v(-34.1, -2.35) * mm, "end": v(-34.02, -2.34) * mm});
            skLineSegment(sketch, "E264", {"start": v(-34.02, -2.34) * mm, "end": v(-33.73, -2.34) * mm});
            skLineSegment(sketch, "E265", {"start": v(-33.73, -2.34) * mm, "end": v(-33.13, -2.34) * mm});
            skLineSegment(sketch, "E266", {"start": v(-33.13, -2.34) * mm, "end": v(-32.42, -2.34) * mm});
            skLineSegment(sketch, "E267", {"start": v(-32.42, -2.34) * mm, "end": v(-31.8, -2.34) * mm});
            skLineSegment(sketch, "E268", {"start": v(-31.8, -2.34) * mm, "end": v(-31.5, -2.34) * mm});
            skLineSegment(sketch, "E269", {"start": v(-31.5, -2.34) * mm, "end": v(-31.38, -2.35) * mm});
            skLineSegment(sketch, "E270", {"start": v(-31.38, -2.35) * mm, "end": v(-31.23, -2.37) * mm});
            skLineSegment(sketch, "E271", {"start": v(-31.23, -2.37) * mm, "end": v(-31.08, -2.4) * mm});
            skLineSegment(sketch, "E272", {"start": v(-31.08, -2.4) * mm, "end": v(-30.94, -2.45) * mm});
            skLineSegment(sketch, "E273", {"start": v(-30.94, -2.45) * mm, "end": v(-30.79, -2.5) * mm});
            skLineSegment(sketch, "E274", {"start": v(-30.79, -2.5) * mm, "end": v(-30.64, -2.58) * mm});
            skLineSegment(sketch, "E275", {"start": v(-30.64, -2.58) * mm, "end": v(-30.5, -2.67) * mm});
            skLineSegment(sketch, "E276", {"start": v(-30.5, -2.67) * mm, "end": v(-30.37, -2.78) * mm});
            skLineSegment(sketch, "E277", {"start": v(-30.37, -2.78) * mm, "end": v(-30.26, -2.9) * mm});
            skLineSegment(sketch, "E278", {"start": v(-30.26, -2.9) * mm, "end": v(-30.17, -3.03) * mm});
            skLineSegment(sketch, "E279", {"start": v(-30.17, -3.03) * mm, "end": v(-30.08, -3.18) * mm});
            skLineSegment(sketch, "E280", {"start": v(-30.08, -3.18) * mm, "end": v(-30.01, -3.34) * mm});
            skLineSegment(sketch, "E281", {"start": v(-30.01, -3.34) * mm, "end": v(-29.96, -3.5) * mm});
            skLineSegment(sketch, "E282", {"start": v(-29.96, -3.5) * mm, "end": v(-29.92, -3.68) * mm});
            skLineSegment(sketch, "E283", {"start": v(-29.92, -3.68) * mm, "end": v(-29.9, -3.85) * mm});
            skLineSegment(sketch, "E284", {"start": v(-29.9, -3.85) * mm, "end": v(-29.9, -4.05) * mm});
            skLineSegment(sketch, "E285", {"start": v(-29.9, -4.05) * mm, "end": v(-29.91, -4.37) * mm});
            skLineSegment(sketch, "E286", {"start": v(-29.91, -4.37) * mm, "end": v(-29.97, -4.66) * mm});
            skLineSegment(sketch, "E287", {"start": v(-29.97, -4.66) * mm, "end": v(-30.06, -4.91) * mm});
            skLineSegment(sketch, "E288", {"start": v(-30.06, -4.91) * mm, "end": v(-30.2, -5.13) * mm});
            skLineSegment(sketch, "E289", {"start": v(-30.2, -5.13) * mm, "end": v(-30.36, -5.31) * mm});
            skLineSegment(sketch, "E290", {"start": v(-30.36, -5.31) * mm, "end": v(-30.55, -5.46) * mm});
            skLineSegment(sketch, "E291", {"start": v(-30.55, -5.46) * mm, "end": v(-30.74, -5.58) * mm});
            skLineSegment(sketch, "E292", {"start": v(-30.74, -5.58) * mm, "end": v(-30.94, -5.67) * mm});
            skLineSegment(sketch, "E293", {"start": v(-30.94, -5.67) * mm, "end": v(-31.14, -5.73) * mm});
            skLineSegment(sketch, "E294", {"start": v(-31.14, -5.73) * mm, "end": v(-31.35, -5.76) * mm});
            skLineSegment(sketch, "E295", {"start": v(-31.35, -5.76) * mm, "end": v(-31.52, -5.76) * mm});
            skLineSegment(sketch, "E296", {"start": v(-31.52, -5.76) * mm, "end": v(-31.97, -5.76) * mm});
            skLineSegment(sketch, "E297", {"start": v(-31.97, -5.76) * mm, "end": v(-32.66, -5.76) * mm});
            skLineSegment(sketch, "E298", {"start": v(-32.66, -5.76) * mm, "end": v(-33.37, -5.76) * mm});
            skLineSegment(sketch, "E299", {"start": v(-33.37, -5.76) * mm, "end": v(-33.88, -5.76) * mm});
            skLineSegment(sketch, "E300", {"start": v(-33.88, -5.76) * mm, "end": v(-34.05, -5.76) * mm});
            skLineSegment(sketch, "E301", {"start": v(-34.05, -5.76) * mm, "end": v(-34.14, -5.74) * mm});
            skLineSegment(sketch, "E302", {"start": v(-34.14, -5.74) * mm, "end": v(-34.21, -5.7) * mm});
            skLineSegment(sketch, "E303", {"start": v(-34.21, -5.7) * mm, "end": v(-34.28, -5.63) * mm});
            skLineSegment(sketch, "E304", {"start": v(-34.28, -5.63) * mm, "end": v(-34.31, -5.55) * mm});
            skLineSegment(sketch, "E305", {"start": v(-34.31, -5.55) * mm, "end": v(-34.33, -5.45) * mm});
            skLineSegment(sketch, "E306", {"start": v(-34.33, -1.42) * mm, "end": v(-34.33, -1.3) * mm});
            skLineSegment(sketch, "E307", {"start": v(-34.33, -1.3) * mm, "end": v(-34.33, -0.98) * mm});
            skLineSegment(sketch, "E308", {"start": v(-34.33, -0.98) * mm, "end": v(-34.33, -0.54) * mm});
            skLineSegment(sketch, "E309", {"start": v(-34.33, -0.54) * mm, "end": v(-34.33, -0.05) * mm});
            skLineSegment(sketch, "E310", {"start": v(-34.33, -0.05) * mm, "end": v(-34.33, 0.4) * mm});
            skLineSegment(sketch, "E311", {"start": v(-34.33, 0.4) * mm, "end": v(-34.33, 0.74) * mm});
            skLineSegment(sketch, "E312", {"start": v(-34.33, 0.74) * mm, "end": v(-34.33, 0.9) * mm});
            skLineSegment(sketch, "E313", {"start": v(-34.33, 0.9) * mm, "end": v(-34.32, 0.96) * mm});
            skLineSegment(sketch, "E314", {"start": v(-34.32, 0.96) * mm, "end": v(-34.3, 1.03) * mm});
            skLineSegment(sketch, "E315", {"start": v(-34.3, 1.03) * mm, "end": v(-34.27, 1.09) * mm});
            skLineSegment(sketch, "E316", {"start": v(-34.27, 1.09) * mm, "end": v(-34.22, 1.14) * mm});
            skLineSegment(sketch, "E317", {"start": v(-34.22, 1.14) * mm, "end": v(-34.17, 1.17) * mm});
            skLineSegment(sketch, "E318", {"start": v(-34.17, 1.17) * mm, "end": v(-34.1, 1.2) * mm});
            skLineSegment(sketch, "E319", {"start": v(-34.1, 1.2) * mm, "end": v(-34.04, 1.21) * mm});
            skLineSegment(sketch, "E320", {"start": v(-34.04, 1.21) * mm, "end": v(-34.01, 1.21) * mm});
            skLineSegment(sketch, "E321", {"start": v(-34.01, 1.21) * mm, "end": v(-33.97, 1.21) * mm});
            skLineSegment(sketch, "E322", {"start": v(-33.97, 1.21) * mm, "end": v(-33.92, 1.21) * mm});
            skLineSegment(sketch, "E323", {"start": v(-33.92, 1.21) * mm, "end": v(-33.85, 1.21) * mm});
            skLineSegment(sketch, "E324", {"start": v(-33.85, 1.21) * mm, "end": v(-33.8, 1.21) * mm});
            skLineSegment(sketch, "E325", {"start": v(-33.8, 1.21) * mm, "end": v(-33.74, 1.21) * mm});
            skLineSegment(sketch, "E326", {"start": v(-33.74, 1.21) * mm, "end": v(-33.71, 1.21) * mm});
            skLineSegment(sketch, "E327", {"start": v(-33.71, 1.21) * mm, "end": v(-33.67, 1.21) * mm});
            skLineSegment(sketch, "E328", {"start": v(-33.67, 1.21) * mm, "end": v(-33.6, 1.2) * mm});
            skLineSegment(sketch, "E329", {"start": v(-33.6, 1.2) * mm, "end": v(-33.54, 1.16) * mm});
            skLineSegment(sketch, "E330", {"start": v(-33.54, 1.16) * mm, "end": v(-33.49, 1.12) * mm});
            skLineSegment(sketch, "E331", {"start": v(-33.49, 1.12) * mm, "end": v(-33.45, 1.07) * mm});
            skLineSegment(sketch, "E332", {"start": v(-33.45, 1.07) * mm, "end": v(-33.42, 1.01) * mm});
            skLineSegment(sketch, "E333", {"start": v(-33.42, 1.01) * mm, "end": v(-33.4, 0.94) * mm});
            skLineSegment(sketch, "E334", {"start": v(-33.4, 0.94) * mm, "end": v(-33.4, 0.9) * mm});
            skLineSegment(sketch, "E335", {"start": v(-33.4, 0.9) * mm, "end": v(-33.4, 0.83) * mm});
            skLineSegment(sketch, "E336", {"start": v(-33.4, 0.83) * mm, "end": v(-33.4, 0.72) * mm});
            skLineSegment(sketch, "E337", {"start": v(-33.4, 0.72) * mm, "end": v(-33.4, 0.58) * mm});
            skLineSegment(sketch, "E338", {"start": v(-33.4, 0.58) * mm, "end": v(-33.4, 0.43) * mm});
            skLineSegment(sketch, "E339", {"start": v(-33.4, 0.43) * mm, "end": v(-33.4, 0.31) * mm});
            skLineSegment(sketch, "E340", {"start": v(-33.4, 0.31) * mm, "end": v(-33.4, 0.23) * mm});
            skLineSegment(sketch, "E341", {"start": v(-33.4, 0.23) * mm, "end": v(-33.38, 0.2) * mm});
            skLineSegment(sketch, "E342", {"start": v(-33.38, 0.2) * mm, "end": v(-33.13, 0.2) * mm});
            skLineSegment(sketch, "E343", {"start": v(-33.13, 0.2) * mm, "end": v(-32.64, 0.2) * mm});
            skLineSegment(sketch, "E344", {"start": v(-32.64, 0.2) * mm, "end": v(-32.02, 0.2) * mm});
            skLineSegment(sketch, "E345", {"start": v(-32.02, 0.2) * mm, "end": v(-31.37, 0.2) * mm});
            skLineSegment(sketch, "E346", {"start": v(-31.37, 0.2) * mm, "end": v(-30.79, 0.2) * mm});
            skLineSegment(sketch, "E347", {"start": v(-30.79, 0.2) * mm, "end": v(-30.39, 0.2) * mm});
            skLineSegment(sketch, "E348", {"start": v(-30.39, 0.2) * mm, "end": v(-30.25, 0.2) * mm});
            skLineSegment(sketch, "E349", {"start": v(-30.25, 0.2) * mm, "end": v(-30.18, 0.2) * mm});
            skLineSegment(sketch, "E350", {"start": v(-30.18, 0.2) * mm, "end": v(-30.12, 0.18) * mm});
            skLineSegment(sketch, "E351", {"start": v(-30.12, 0.18) * mm, "end": v(-30.06, 0.14) * mm});
            skLineSegment(sketch, "E352", {"start": v(-30.06, 0.14) * mm, "end": v(-30.02, 0.1) * mm});
            skLineSegment(sketch, "E353", {"start": v(-30.02, 0.1) * mm, "end": v(-29.98, 0.03) * mm});
            skLineSegment(sketch, "E354", {"start": v(-29.98, 0.03) * mm, "end": v(-29.96, -0.03) * mm});
            skLineSegment(sketch, "E355", {"start": v(-29.96, -0.03) * mm, "end": v(-29.95, -0.1) * mm});
            skLineSegment(sketch, "E356", {"start": v(-29.95, -0.1) * mm, "end": v(-29.95, -0.16) * mm});
            skLineSegment(sketch, "E357", {"start": v(-29.95, -0.16) * mm, "end": v(-29.95, -0.22) * mm});
            skLineSegment(sketch, "E358", {"start": v(-29.95, -0.22) * mm, "end": v(-29.95, -0.3) * mm});
            skLineSegment(sketch, "E359", {"start": v(-29.95, -0.3) * mm, "end": v(-29.95, -0.35) * mm});
            skLineSegment(sketch, "E360", {"start": v(-29.95, -0.35) * mm, "end": v(-29.95, -0.4) * mm});
            skLineSegment(sketch, "E361", {"start": v(-29.95, -0.4) * mm, "end": v(-29.95, -0.42) * mm});
            skLineSegment(sketch, "E362", {"start": v(-29.95, -0.42) * mm, "end": v(-29.96, -0.48) * mm});
            skLineSegment(sketch, "E363", {"start": v(-29.96, -0.48) * mm, "end": v(-29.98, -0.55) * mm});
            skLineSegment(sketch, "E364", {"start": v(-29.98, -0.55) * mm, "end": v(-30.01, -0.6) * mm});
            skLineSegment(sketch, "E365", {"start": v(-30.01, -0.6) * mm, "end": v(-30.06, -0.66) * mm});
            skLineSegment(sketch, "E366", {"start": v(-30.06, -0.66) * mm, "end": v(-30.11, -0.7) * mm});
            skLineSegment(sketch, "E367", {"start": v(-30.11, -0.7) * mm, "end": v(-30.17, -0.72) * mm});
            skLineSegment(sketch, "E368", {"start": v(-30.17, -0.72) * mm, "end": v(-30.24, -0.73) * mm});
            skLineSegment(sketch, "E369", {"start": v(-30.24, -0.73) * mm, "end": v(-30.35, -0.73) * mm});
            skLineSegment(sketch, "E370", {"start": v(-30.35, -0.73) * mm, "end": v(-30.72, -0.73) * mm});
            skLineSegment(sketch, "E371", {"start": v(-30.72, -0.73) * mm, "end": v(-31.28, -0.73) * mm});
            skLineSegment(sketch, "E372", {"start": v(-31.28, -0.73) * mm, "end": v(-31.92, -0.73) * mm});
            skLineSegment(sketch, "E373", {"start": v(-31.92, -0.73) * mm, "end": v(-32.56, -0.73) * mm});
            skLineSegment(sketch, "E374", {"start": v(-32.56, -0.73) * mm, "end": v(-33.07, -0.73) * mm});
            skLineSegment(sketch, "E375", {"start": v(-33.07, -0.73) * mm, "end": v(-33.37, -0.73) * mm});
            skLineSegment(sketch, "E376", {"start": v(-33.37, -0.73) * mm, "end": v(-33.4, -0.75) * mm});
            skLineSegment(sketch, "E377", {"start": v(-33.4, -0.75) * mm, "end": v(-33.4, -0.82) * mm});
            skLineSegment(sketch, "E378", {"start": v(-33.4, -0.82) * mm, "end": v(-33.4, -0.94) * mm});
            skLineSegment(sketch, "E379", {"start": v(-33.4, -0.94) * mm, "end": v(-33.4, -1.08) * mm});
            skLineSegment(sketch, "E380", {"start": v(-33.4, -1.08) * mm, "end": v(-33.4, -1.22) * mm});
            skLineSegment(sketch, "E381", {"start": v(-33.4, -1.22) * mm, "end": v(-33.4, -1.34) * mm});
            skLineSegment(sketch, "E382", {"start": v(-33.4, -1.34) * mm, "end": v(-33.4, -1.4) * mm});
            skLineSegment(sketch, "E383", {"start": v(-33.4, -1.4) * mm, "end": v(-33.4, -1.45) * mm});
            skLineSegment(sketch, "E384", {"start": v(-33.4, -1.45) * mm, "end": v(-33.42, -1.52) * mm});
            skLineSegment(sketch, "E385", {"start": v(-33.42, -1.52) * mm, "end": v(-33.44, -1.58) * mm});
            skLineSegment(sketch, "E386", {"start": v(-33.44, -1.58) * mm, "end": v(-33.48, -1.63) * mm});
            skLineSegment(sketch, "E387", {"start": v(-33.48, -1.63) * mm, "end": v(-33.53, -1.68) * mm});
            skLineSegment(sketch, "E388", {"start": v(-33.53, -1.68) * mm, "end": v(-33.6, -1.7) * mm});
            skLineSegment(sketch, "E389", {"start": v(-33.6, -1.7) * mm, "end": v(-33.66, -1.73) * mm});
            skLineSegment(sketch, "E390", {"start": v(-33.66, -1.73) * mm, "end": v(-33.7, -1.73) * mm});
            skLineSegment(sketch, "E391", {"start": v(-33.7, -1.73) * mm, "end": v(-33.74, -1.73) * mm});
            skLineSegment(sketch, "E392", {"start": v(-33.74, -1.73) * mm, "end": v(-33.78, -1.73) * mm});
            skLineSegment(sketch, "E393", {"start": v(-33.78, -1.73) * mm, "end": v(-33.85, -1.73) * mm});
            skLineSegment(sketch, "E394", {"start": v(-33.85, -1.73) * mm, "end": v(-33.91, -1.73) * mm});
            skLineSegment(sketch, "E395", {"start": v(-33.91, -1.73) * mm, "end": v(-33.97, -1.73) * mm});
            skLineSegment(sketch, "E396", {"start": v(-33.97, -1.73) * mm, "end": v(-34, -1.73) * mm});
            skLineSegment(sketch, "E397", {"start": v(-34, -1.73) * mm, "end": v(-34.03, -1.73) * mm});
            skLineSegment(sketch, "E398", {"start": v(-34.03, -1.73) * mm, "end": v(-34.1, -1.72) * mm});
            skLineSegment(sketch, "E399", {"start": v(-34.1, -1.72) * mm, "end": v(-34.16, -1.7) * mm});
            skLineSegment(sketch, "E400", {"start": v(-34.16, -1.7) * mm, "end": v(-34.22, -1.66) * mm});
            skLineSegment(sketch, "E401", {"start": v(-34.22, -1.66) * mm, "end": v(-34.26, -1.61) * mm});
            skLineSegment(sketch, "E402", {"start": v(-34.26, -1.61) * mm, "end": v(-34.3, -1.55) * mm});
            skLineSegment(sketch, "E403", {"start": v(-34.3, -1.55) * mm, "end": v(-34.32, -1.5) * mm});
            skLineSegment(sketch, "E404", {"start": v(-34.32, -1.5) * mm, "end": v(-34.33, -1.42) * mm});
            skLineSegment(sketch, "E405", {"start": v(-34.02, 1.83) * mm, "end": v(-34.1, 1.84) * mm});
            skLineSegment(sketch, "E406", {"start": v(-34.1, 1.84) * mm, "end": v(-34.18, 1.87) * mm});
            skLineSegment(sketch, "E407", {"start": v(-34.18, 1.87) * mm, "end": v(-34.24, 1.92) * mm});
            skLineSegment(sketch, "E408", {"start": v(-34.24, 1.92) * mm, "end": v(-34.3, 1.99) * mm});
            skLineSegment(sketch, "E409", {"start": v(-34.3, 1.99) * mm, "end": v(-34.32, 2.06) * mm});
            skLineSegment(sketch, "E410", {"start": v(-34.32, 2.06) * mm, "end": v(-34.33, 2.14) * mm});
            skLineSegment(sketch, "E411", {"start": v(-34.33, 2.14) * mm, "end": v(-34.33, 2.25) * mm});
            skLineSegment(sketch, "E412", {"start": v(-34.33, 2.25) * mm, "end": v(-34.33, 2.47) * mm});
            skLineSegment(sketch, "E413", {"start": v(-34.33, 2.47) * mm, "end": v(-34.33, 2.76) * mm});
            skLineSegment(sketch, "E414", {"start": v(-34.33, 2.76) * mm, "end": v(-34.33, 3.03) * mm});
            skLineSegment(sketch, "E415", {"start": v(-34.33, 3.03) * mm, "end": v(-34.33, 3.22) * mm});
            skLineSegment(sketch, "E416", {"start": v(-34.33, 3.22) * mm, "end": v(-34.33, 3.32) * mm});
            skLineSegment(sketch, "E417", {"start": v(-34.33, 3.32) * mm, "end": v(-34.31, 3.54) * mm});
            skLineSegment(sketch, "E418", {"start": v(-34.31, 3.54) * mm, "end": v(-34.28, 3.73) * mm});
            skLineSegment(sketch, "E419", {"start": v(-34.28, 3.73) * mm, "end": v(-34.22, 3.91) * mm});
            skLineSegment(sketch, "E420", {"start": v(-34.22, 3.91) * mm, "end": v(-34.15, 4.08) * mm});
            skLineSegment(sketch, "E421", {"start": v(-34.15, 4.08) * mm, "end": v(-34.05, 4.22) * mm});
            skLineSegment(sketch, "E422", {"start": v(-34.05, 4.22) * mm, "end": v(-33.94, 4.36) * mm});
            skLineSegment(sketch, "E423", {"start": v(-33.94, 4.36) * mm, "end": v(-33.81, 4.47) * mm});
            skLineSegment(sketch, "E424", {"start": v(-33.81, 4.47) * mm, "end": v(-33.67, 4.56) * mm});
            skLineSegment(sketch, "E425", {"start": v(-33.67, 4.56) * mm, "end": v(-33.5, 4.62) * mm});
            skLineSegment(sketch, "E426", {"start": v(-33.5, 4.62) * mm, "end": v(-33.34, 4.67) * mm});
            skLineSegment(sketch, "E427", {"start": v(-33.34, 4.67) * mm, "end": v(-33.15, 4.69) * mm});
            skLineSegment(sketch, "E428", {"start": v(-33.15, 4.69) * mm, "end": v(-33, 4.7) * mm});
            skLineSegment(sketch, "E429", {"start": v(-33, 4.7) * mm, "end": v(-32.88, 4.68) * mm});
            skLineSegment(sketch, "E430", {"start": v(-32.88, 4.68) * mm, "end": v(-32.76, 4.66) * mm});
            skLineSegment(sketch, "E431", {"start": v(-32.76, 4.66) * mm, "end": v(-32.64, 4.63) * mm});
            skLineSegment(sketch, "E432", {"start": v(-32.64, 4.63) * mm, "end": v(-32.52, 4.6) * mm});
            skLineSegment(sketch, "E433", {"start": v(-32.52, 4.6) * mm, "end": v(-32.4, 4.54) * mm});
            skLineSegment(sketch, "E434", {"start": v(-32.4, 4.54) * mm, "end": v(-32.28, 4.48) * mm});
            skLineSegment(sketch, "E435", {"start": v(-32.28, 4.48) * mm, "end": v(-32.16, 4.4) * mm});
            skLineSegment(sketch, "E436", {"start": v(-32.16, 4.4) * mm, "end": v(-32.06, 4.3) * mm});
            skLineSegment(sketch, "E437", {"start": v(-32.06, 4.3) * mm, "end": v(-31.96, 4.2) * mm});
            skLineSegment(sketch, "E438", {"start": v(-31.96, 4.2) * mm, "end": v(-31.88, 4.06) * mm});
            skLineSegment(sketch, "E439", {"start": v(-31.88, 4.06) * mm, "end": v(-31.8, 3.92) * mm});
            skLineSegment(sketch, "E440", {"start": v(-31.8, 3.92) * mm, "end": v(-31.72, 3.9) * mm});
            skLineSegment(sketch, "E441", {"start": v(-31.72, 3.9) * mm, "end": v(-31.5, 4.05) * mm});
            skLineSegment(sketch, "E442", {"start": v(-31.5, 4.05) * mm, "end": v(-31.19, 4.27) * mm});
            skLineSegment(sketch, "E443", {"start": v(-31.19, 4.27) * mm, "end": v(-30.85, 4.5) * mm});
            skLineSegment(sketch, "E444", {"start": v(-30.85, 4.5) * mm, "end": v(-30.57, 4.68) * mm});
            skLineSegment(sketch, "E445", {"start": v(-30.57, 4.68) * mm, "end": v(-30.44, 4.77) * mm});
            skLineSegment(sketch, "E446", {"start": v(-30.44, 4.77) * mm, "end": v(-30.35, 4.81) * mm});
            skLineSegment(sketch, "E447", {"start": v(-30.35, 4.81) * mm, "end": v(-30.23, 4.82) * mm});
            skLineSegment(sketch, "E448", {"start": v(-30.23, 4.82) * mm, "end": v(-30.13, 4.8) * mm});
            skLineSegment(sketch, "E449", {"start": v(-30.13, 4.8) * mm, "end": v(-30.04, 4.73) * mm});
            skLineSegment(sketch, "E450", {"start": v(-30.04, 4.73) * mm, "end": v(-29.98, 4.64) * mm});
            skLineSegment(sketch, "E451", {"start": v(-29.98, 4.64) * mm, "end": v(-29.95, 4.52) * mm});
            skLineSegment(sketch, "E452", {"start": v(-29.95, 4.52) * mm, "end": v(-29.95, 4.5) * mm});
            skLineSegment(sketch, "E453", {"start": v(-29.95, 4.5) * mm, "end": v(-29.95, 4.43) * mm});
            skLineSegment(sketch, "E454", {"start": v(-29.95, 4.43) * mm, "end": v(-29.95, 4.35) * mm});
            skLineSegment(sketch, "E455", {"start": v(-29.95, 4.35) * mm, "end": v(-29.95, 4.26) * mm});
            skLineSegment(sketch, "E456", {"start": v(-29.95, 4.26) * mm, "end": v(-29.95, 4.2) * mm});
            skLineSegment(sketch, "E457", {"start": v(-29.95, 4.2) * mm, "end": v(-29.95, 4.17) * mm});
            skLineSegment(sketch, "E458", {"start": v(-29.95, 4.17) * mm, "end": v(-29.96, 4.12) * mm});
            skLineSegment(sketch, "E459", {"start": v(-29.96, 4.12) * mm, "end": v(-29.97, 4.07) * mm});
            skLineSegment(sketch, "E460", {"start": v(-29.97, 4.07) * mm, "end": v(-30, 4.03) * mm});
            skLineSegment(sketch, "E461", {"start": v(-30, 4.03) * mm, "end": v(-30.02, 3.98) * mm});
            skLineSegment(sketch, "E462", {"start": v(-30.02, 3.98) * mm, "end": v(-30.06, 3.95) * mm});
            skLineSegment(sketch, "E463", {"start": v(-30.06, 3.95) * mm, "end": v(-30.1, 3.92) * mm});
            skLineSegment(sketch, "E464", {"start": v(-30.1, 3.92) * mm, "end": v(-30.25, 3.81) * mm});
            skLineSegment(sketch, "E465", {"start": v(-30.25, 3.81) * mm, "end": v(-30.57, 3.6) * mm});
            skLineSegment(sketch, "E466", {"start": v(-30.57, 3.6) * mm, "end": v(-30.96, 3.34) * mm});
            skLineSegment(sketch, "E467", {"start": v(-30.96, 3.34) * mm, "end": v(-31.33, 3.1) * mm});
            skLineSegment(sketch, "E468", {"start": v(-31.33, 3.1) * mm, "end": v(-31.58, 2.92) * mm});
            skLineSegment(sketch, "E469", {"start": v(-31.58, 2.92) * mm, "end": v(-31.65, 2.88) * mm});
            skLineSegment(sketch, "E470", {"start": v(-31.65, 2.88) * mm, "end": v(-31.65, 2.84) * mm});
            skLineSegment(sketch, "E471", {"start": v(-31.65, 2.84) * mm, "end": v(-31.65, 2.82) * mm});
            skLineSegment(sketch, "E472", {"start": v(-31.65, 2.82) * mm, "end": v(-31.65, 2.8) * mm});
            skLineSegment(sketch, "E473", {"start": v(-31.65, 2.8) * mm, "end": v(-31.63, 2.77) * mm});
            skLineSegment(sketch, "E474", {"start": v(-31.63, 2.77) * mm, "end": v(-31.45, 2.77) * mm});
            skLineSegment(sketch, "E475", {"start": v(-31.45, 2.77) * mm, "end": v(-31.14, 2.77) * mm});
            skLineSegment(sketch, "E476", {"start": v(-31.14, 2.77) * mm, "end": v(-30.79, 2.77) * mm});
            skLineSegment(sketch, "E477", {"start": v(-30.79, 2.77) * mm, "end": v(-30.48, 2.77) * mm});
            skLineSegment(sketch, "E478", {"start": v(-30.48, 2.77) * mm, "end": v(-30.29, 2.77) * mm});
            skLineSegment(sketch, "E479", {"start": v(-30.29, 2.77) * mm, "end": v(-30.22, 2.77) * mm});
            skLineSegment(sketch, "E480", {"start": v(-30.22, 2.77) * mm, "end": v(-30.14, 2.75) * mm});
            skLineSegment(sketch, "E481", {"start": v(-30.14, 2.75) * mm, "end": v(-30.07, 2.7) * mm});
            skLineSegment(sketch, "E482", {"start": v(-30.07, 2.7) * mm, "end": v(-30.01, 2.65) * mm});
            skLineSegment(sketch, "E483", {"start": v(-30.01, 2.65) * mm, "end": v(-29.97, 2.58) * mm});
            skLineSegment(sketch, "E484", {"start": v(-29.97, 2.58) * mm, "end": v(-29.95, 2.5) * mm});
            skLineSegment(sketch, "E485", {"start": v(-29.95, 2.5) * mm, "end": v(-29.95, 2.45) * mm});
            skLineSegment(sketch, "E486", {"start": v(-29.95, 2.45) * mm, "end": v(-29.95, 2.4) * mm});
            skLineSegment(sketch, "E487", {"start": v(-29.95, 2.4) * mm, "end": v(-29.95, 2.33) * mm});
            skLineSegment(sketch, "E488", {"start": v(-29.95, 2.33) * mm, "end": v(-29.95, 2.24) * mm});
            skLineSegment(sketch, "E489", {"start": v(-29.95, 2.24) * mm, "end": v(-29.95, 2.18) * mm});
            skLineSegment(sketch, "E490", {"start": v(-29.95, 2.18) * mm, "end": v(-29.95, 2.14) * mm});
            skLineSegment(sketch, "E491", {"start": v(-29.95, 2.14) * mm, "end": v(-29.96, 2.07) * mm});
            skLineSegment(sketch, "E492", {"start": v(-29.96, 2.07) * mm, "end": v(-29.99, 2) * mm});
            skLineSegment(sketch, "E493", {"start": v(-29.99, 2) * mm, "end": v(-30.03, 1.93) * mm});
            skLineSegment(sketch, "E494", {"start": v(-30.03, 1.93) * mm, "end": v(-30.1, 1.88) * mm});
            skLineSegment(sketch, "E495", {"start": v(-30.1, 1.88) * mm, "end": v(-30.17, 1.84) * mm});
            skLineSegment(sketch, "E496", {"start": v(-30.17, 1.84) * mm, "end": v(-30.25, 1.83) * mm});
            skLineSegment(sketch, "E497", {"start": v(-30.25, 1.83) * mm, "end": v(-30.5, 1.83) * mm});
            skLineSegment(sketch, "E498", {"start": v(-30.5, 1.83) * mm, "end": v(-31.17, 1.83) * mm});
            skLineSegment(sketch, "E499", {"start": v(-31.17, 1.83) * mm, "end": v(-32.08, 1.83) * mm});
            skLineSegment(sketch, "E500", {"start": v(-32.08, 1.83) * mm, "end": v(-33.01, 1.83) * mm});
            skLineSegment(sketch, "E501", {"start": v(-33.01, 1.83) * mm, "end": v(-33.73, 1.83) * mm});
            skLineSegment(sketch, "E502", {"start": v(-33.73, 1.83) * mm, "end": v(-34.02, 1.83) * mm});
            skLineSegment(sketch, "E503", {"start": v(-33.55, 2.78) * mm, "end": v(-33.5, 2.78) * mm});
            skLineSegment(sketch, "E504", {"start": v(-33.5, 2.78) * mm, "end": v(-33.38, 2.78) * mm});
            skLineSegment(sketch, "E505", {"start": v(-33.38, 2.78) * mm, "end": v(-33.2, 2.78) * mm});
            skLineSegment(sketch, "E506", {"start": v(-33.2, 2.78) * mm, "end": v(-33, 2.78) * mm});
            skLineSegment(sketch, "E507", {"start": v(-33, 2.78) * mm, "end": v(-32.8, 2.78) * mm});
            skLineSegment(sketch, "E508", {"start": v(-32.8, 2.78) * mm, "end": v(-32.6, 2.78) * mm});
            skLineSegment(sketch, "E509", {"start": v(-32.6, 2.78) * mm, "end": v(-32.47, 2.78) * mm});
            skLineSegment(sketch, "E510", {"start": v(-32.47, 2.78) * mm, "end": v(-32.41, 2.78) * mm});
            skLineSegment(sketch, "E511", {"start": v(-32.41, 2.78) * mm, "end": v(-32.4, 2.8) * mm});
            skLineSegment(sketch, "E512", {"start": v(-32.4, 2.8) * mm, "end": v(-32.4, 2.84) * mm});
            skLineSegment(sketch, "E513", {"start": v(-32.4, 2.84) * mm, "end": v(-32.4, 2.87) * mm});
            skLineSegment(sketch, "E514", {"start": v(-32.4, 2.87) * mm, "end": v(-32.4, 2.9) * mm});
            skLineSegment(sketch, "E515", {"start": v(-32.4, 2.9) * mm, "end": v(-32.4, 2.94) * mm});
            skLineSegment(sketch, "E516", {"start": v(-32.4, 2.94) * mm, "end": v(-32.4, 2.97) * mm});
            skLineSegment(sketch, "E517", {"start": v(-32.4, 2.97) * mm, "end": v(-32.41, 3.1) * mm});
            skLineSegment(sketch, "E518", {"start": v(-32.41, 3.1) * mm, "end": v(-32.43, 3.25) * mm});
            skLineSegment(sketch, "E519", {"start": v(-32.43, 3.25) * mm, "end": v(-32.47, 3.39) * mm});
            skLineSegment(sketch, "E520", {"start": v(-32.47, 3.39) * mm, "end": v(-32.53, 3.5) * mm});
            skLineSegment(sketch, "E521", {"start": v(-32.53, 3.5) * mm, "end": v(-32.6, 3.59) * mm});
            skLineSegment(sketch, "E522", {"start": v(-32.6, 3.59) * mm, "end": v(-32.7, 3.65) * mm});
            skLineSegment(sketch, "E523", {"start": v(-32.7, 3.65) * mm, "end": v(-32.81, 3.7) * mm});
            skLineSegment(sketch, "E524", {"start": v(-32.81, 3.7) * mm, "end": v(-32.94, 3.72) * mm});
            skLineSegment(sketch, "E525", {"start": v(-32.94, 3.72) * mm, "end": v(-33.04, 3.72) * mm});
            skLineSegment(sketch, "E526", {"start": v(-33.04, 3.72) * mm, "end": v(-33.1, 3.72) * mm});
            skLineSegment(sketch, "E527", {"start": v(-33.1, 3.72) * mm, "end": v(-33.15, 3.7) * mm});
            skLineSegment(sketch, "E528", {"start": v(-33.15, 3.7) * mm, "end": v(-33.2, 3.69) * mm});
            skLineSegment(sketch, "E529", {"start": v(-33.2, 3.69) * mm, "end": v(-33.25, 3.66) * mm});
            skLineSegment(sketch, "E530", {"start": v(-33.25, 3.66) * mm, "end": v(-33.3, 3.64) * mm});
            skLineSegment(sketch, "E531", {"start": v(-33.3, 3.64) * mm, "end": v(-33.34, 3.6) * mm});
            skLineSegment(sketch, "E532", {"start": v(-33.34, 3.6) * mm, "end": v(-33.38, 3.56) * mm});
            skLineSegment(sketch, "E533", {"start": v(-33.38, 3.56) * mm, "end": v(-33.42, 3.51) * mm});
            skLineSegment(sketch, "E534", {"start": v(-33.42, 3.51) * mm, "end": v(-33.45, 3.46) * mm});
            skLineSegment(sketch, "E535", {"start": v(-33.45, 3.46) * mm, "end": v(-33.48, 3.4) * mm});
            skLineSegment(sketch, "E536", {"start": v(-33.48, 3.4) * mm, "end": v(-33.5, 3.35) * mm});
            skLineSegment(sketch, "E537", {"start": v(-33.5, 3.35) * mm, "end": v(-33.52, 3.28) * mm});
            skLineSegment(sketch, "E538", {"start": v(-33.52, 3.28) * mm, "end": v(-33.53, 3.22) * mm});
            skLineSegment(sketch, "E539", {"start": v(-33.53, 3.22) * mm, "end": v(-33.54, 3.14) * mm});
            skLineSegment(sketch, "E540", {"start": v(-33.54, 3.14) * mm, "end": v(-33.55, 3.07) * mm});
            skLineSegment(sketch, "E541", {"start": v(-33.55, 3.07) * mm, "end": v(-33.55, 3) * mm});
            skLineSegment(sketch, "E542", {"start": v(-33.55, 3) * mm, "end": v(-33.55, 2.96) * mm});
            skLineSegment(sketch, "E543", {"start": v(-33.55, 2.96) * mm, "end": v(-33.55, 2.92) * mm});
            skLineSegment(sketch, "E544", {"start": v(-33.55, 2.92) * mm, "end": v(-33.55, 2.88) * mm});
            skLineSegment(sketch, "E545", {"start": v(-33.55, 2.88) * mm, "end": v(-33.55, 2.85) * mm});
            skLineSegment(sketch, "E546", {"start": v(-33.55, 2.85) * mm, "end": v(-33.55, 2.81) * mm});
            skLineSegment(sketch, "E547", {"start": v(-33.55, 2.81) * mm, "end": v(-33.55, 2.78) * mm});
            skLineSegment(sketch, "E548", {"start": v(-32.14, 5.4) * mm, "end": v(-32.38, 5.41) * mm});
            skLineSegment(sketch, "E549", {"start": v(-32.38, 5.41) * mm, "end": v(-32.6, 5.44) * mm});
            skLineSegment(sketch, "E550", {"start": v(-32.6, 5.44) * mm, "end": v(-32.81, 5.5) * mm});
            skLineSegment(sketch, "E551", {"start": v(-32.81, 5.5) * mm, "end": v(-33.02, 5.56) * mm});
            skLineSegment(sketch, "E552", {"start": v(-33.02, 5.56) * mm, "end": v(-33.2, 5.65) * mm});
            skLineSegment(sketch, "E553", {"start": v(-33.2, 5.65) * mm, "end": v(-33.4, 5.75) * mm});
            skLineSegment(sketch, "E554", {"start": v(-33.4, 5.75) * mm, "end": v(-33.56, 5.88) * mm});
            skLineSegment(sketch, "E555", {"start": v(-33.56, 5.88) * mm, "end": v(-33.72, 6.02) * mm});
            skLineSegment(sketch, "E556", {"start": v(-33.72, 6.02) * mm, "end": v(-33.87, 6.19) * mm});
            skLineSegment(sketch, "E557", {"start": v(-33.87, 6.19) * mm, "end": v(-34, 6.35) * mm});
            skLineSegment(sketch, "E558", {"start": v(-34, 6.35) * mm, "end": v(-34.11, 6.53) * mm});
            skLineSegment(sketch, "E559", {"start": v(-34.11, 6.53) * mm, "end": v(-34.2, 6.71) * mm});
            skLineSegment(sketch, "E560", {"start": v(-34.2, 6.71) * mm, "end": v(-34.27, 6.9) * mm});
            skLineSegment(sketch, "E561", {"start": v(-34.27, 6.9) * mm, "end": v(-34.33, 7.1) * mm});
            skLineSegment(sketch, "E562", {"start": v(-34.33, 7.1) * mm, "end": v(-34.36, 7.3) * mm});
            skLineSegment(sketch, "E563", {"start": v(-34.36, 7.3) * mm, "end": v(-34.38, 7.51) * mm});
            skLineSegment(sketch, "E564", {"start": v(-34.38, 7.51) * mm, "end": v(-34.37, 7.74) * mm});
            skLineSegment(sketch, "E565", {"start": v(-34.37, 7.74) * mm, "end": v(-34.35, 7.97) * mm});
            skLineSegment(sketch, "E566", {"start": v(-34.35, 7.97) * mm, "end": v(-34.3, 8.19) * mm});
            skLineSegment(sketch, "E567", {"start": v(-34.3, 8.19) * mm, "end": v(-34.24, 8.4) * mm});
            skLineSegment(sketch, "E568", {"start": v(-34.24, 8.4) * mm, "end": v(-34.16, 8.59) * mm});
            skLineSegment(sketch, "E569", {"start": v(-34.16, 8.59) * mm, "end": v(-34.06, 8.77) * mm});
            skLineSegment(sketch, "E570", {"start": v(-34.06, 8.77) * mm, "end": v(-33.94, 8.95) * mm});
            skLineSegment(sketch, "E571", {"start": v(-33.94, 8.95) * mm, "end": v(-33.8, 9.12) * mm});
            skLineSegment(sketch, "E572", {"start": v(-33.8, 9.12) * mm, "end": v(-33.64, 9.27) * mm});
            skLineSegment(sketch, "E573", {"start": v(-33.64, 9.27) * mm, "end": v(-33.47, 9.4) * mm});
            skLineSegment(sketch, "E574", {"start": v(-33.47, 9.4) * mm, "end": v(-33.3, 9.52) * mm});
            skLineSegment(sketch, "E575", {"start": v(-33.3, 9.52) * mm, "end": v(-33.1, 9.62) * mm});
            skLineSegment(sketch, "E576", {"start": v(-33.1, 9.62) * mm, "end": v(-32.9, 9.7) * mm});
            skLineSegment(sketch, "E577", {"start": v(-32.9, 9.7) * mm, "end": v(-32.7, 9.75) * mm});
            skLineSegment(sketch, "E578", {"start": v(-32.7, 9.75) * mm, "end": v(-32.48, 9.8) * mm});
            skLineSegment(sketch, "E579", {"start": v(-32.48, 9.8) * mm, "end": v(-32.25, 9.8) * mm});
            skLineSegment(sketch, "E580", {"start": v(-32.25, 9.8) * mm, "end": v(-32.02, 9.8) * mm});
            skLineSegment(sketch, "E581", {"start": v(-32.02, 9.8) * mm, "end": v(-31.8, 9.8) * mm});
            skLineSegment(sketch, "E582", {"start": v(-31.8, 9.8) * mm, "end": v(-31.57, 9.75) * mm});
            skLineSegment(sketch, "E583", {"start": v(-31.57, 9.75) * mm, "end": v(-31.37, 9.7) * mm});
            skLineSegment(sketch, "E584", {"start": v(-31.37, 9.7) * mm, "end": v(-31.17, 9.62) * mm});
            skLineSegment(sketch, "E585", {"start": v(-31.17, 9.62) * mm, "end": v(-30.98, 9.52) * mm});
            skLineSegment(sketch, "E586", {"start": v(-30.98, 9.52) * mm, "end": v(-30.8, 9.4) * mm});
            skLineSegment(sketch, "E587", {"start": v(-30.8, 9.4) * mm, "end": v(-30.64, 9.28) * mm});
            skLineSegment(sketch, "E588", {"start": v(-30.64, 9.28) * mm, "end": v(-30.48, 9.12) * mm});
            skLineSegment(sketch, "E589", {"start": v(-30.48, 9.12) * mm, "end": v(-30.34, 8.96) * mm});
            skLineSegment(sketch, "E590", {"start": v(-30.34, 8.96) * mm, "end": v(-30.22, 8.79) * mm});
            skLineSegment(sketch, "E591", {"start": v(-30.22, 8.79) * mm, "end": v(-30.12, 8.6) * mm});
            skLineSegment(sketch, "E592", {"start": v(-30.12, 8.6) * mm, "end": v(-30.04, 8.4) * mm});
            skLineSegment(sketch, "E593", {"start": v(-30.04, 8.4) * mm, "end": v(-29.97, 8.2) * mm});
            skLineSegment(sketch, "E594", {"start": v(-29.97, 8.2) * mm, "end": v(-29.93, 8) * mm});
            skLineSegment(sketch, "E595", {"start": v(-29.93, 8) * mm, "end": v(-29.9, 7.77) * mm});
            skLineSegment(sketch, "E596", {"start": v(-29.9, 7.77) * mm, "end": v(-29.9, 7.54) * mm});
            skLineSegment(sketch, "E597", {"start": v(-29.9, 7.54) * mm, "end": v(-29.91, 7.3) * mm});
            skLineSegment(sketch, "E598", {"start": v(-29.91, 7.3) * mm, "end": v(-29.95, 7.1) * mm});
            skLineSegment(sketch, "E599", {"start": v(-29.95, 7.1) * mm, "end": v(-30, 6.88) * mm});
            skLineSegment(sketch, "E600", {"start": v(-30, 6.88) * mm, "end": v(-30.07, 6.69) * mm});
            skLineSegment(sketch, "E601", {"start": v(-30.07, 6.69) * mm, "end": v(-30.16, 6.5) * mm});
            skLineSegment(sketch, "E602", {"start": v(-30.16, 6.5) * mm, "end": v(-30.27, 6.32) * mm});
            skLineSegment(sketch, "E603", {"start": v(-30.27, 6.32) * mm, "end": v(-30.4, 6.16) * mm});
            skLineSegment(sketch, "E604", {"start": v(-30.4, 6.16) * mm, "end": v(-30.55, 6) * mm});
            skLineSegment(sketch, "E605", {"start": v(-30.55, 6) * mm, "end": v(-30.71, 5.86) * mm});
            skLineSegment(sketch, "E606", {"start": v(-30.71, 5.86) * mm, "end": v(-30.89, 5.74) * mm});
            skLineSegment(sketch, "E607", {"start": v(-30.89, 5.74) * mm, "end": v(-31.07, 5.64) * mm});
            skLineSegment(sketch, "E608", {"start": v(-31.07, 5.64) * mm, "end": v(-31.26, 5.55) * mm});
            skLineSegment(sketch, "E609", {"start": v(-31.26, 5.55) * mm, "end": v(-31.47, 5.49) * mm});
            skLineSegment(sketch, "E610", {"start": v(-31.47, 5.49) * mm, "end": v(-31.68, 5.44) * mm});
            skLineSegment(sketch, "E611", {"start": v(-31.68, 5.44) * mm, "end": v(-31.9, 5.41) * mm});
            skLineSegment(sketch, "E612", {"start": v(-31.9, 5.41) * mm, "end": v(-32.14, 5.4) * mm});
            skLineSegment(sketch, "E613", {"start": v(-33.5, 7.6) * mm, "end": v(-33.5, 7.48) * mm});
            skLineSegment(sketch, "E614", {"start": v(-33.5, 7.48) * mm, "end": v(-33.48, 7.35) * mm});
            skLineSegment(sketch, "E615", {"start": v(-33.48, 7.35) * mm, "end": v(-33.46, 7.23) * mm});
            skLineSegment(sketch, "E616", {"start": v(-33.46, 7.23) * mm, "end": v(-33.42, 7.12) * mm});
            skLineSegment(sketch, "E617", {"start": v(-33.42, 7.12) * mm, "end": v(-33.36, 7.01) * mm});
            skLineSegment(sketch, "E618", {"start": v(-33.36, 7.01) * mm, "end": v(-33.3, 6.91) * mm});
            skLineSegment(sketch, "E619", {"start": v(-33.3, 6.91) * mm, "end": v(-33.22, 6.82) * mm});
            skLineSegment(sketch, "E620", {"start": v(-33.22, 6.82) * mm, "end": v(-33.13, 6.73) * mm});
            skLineSegment(sketch, "E621", {"start": v(-33.13, 6.73) * mm, "end": v(-33.04, 6.65) * mm});
            skLineSegment(sketch, "E622", {"start": v(-33.04, 6.65) * mm, "end": v(-32.93, 6.59) * mm});
            skLineSegment(sketch, "E623", {"start": v(-32.93, 6.59) * mm, "end": v(-32.82, 6.53) * mm});
            skLineSegment(sketch, "E624", {"start": v(-32.82, 6.53) * mm, "end": v(-32.7, 6.48) * mm});
            skLineSegment(sketch, "E625", {"start": v(-32.7, 6.48) * mm, "end": v(-32.57, 6.44) * mm});
            skLineSegment(sketch, "E626", {"start": v(-32.57, 6.44) * mm, "end": v(-32.44, 6.41) * mm});
            skLineSegment(sketch, "E627", {"start": v(-32.44, 6.41) * mm, "end": v(-32.3, 6.4) * mm});
            skLineSegment(sketch, "E628", {"start": v(-32.3, 6.4) * mm, "end": v(-32.15, 6.39) * mm});
            skLineSegment(sketch, "E629", {"start": v(-32.15, 6.39) * mm, "end": v(-32.01, 6.39) * mm});
            skLineSegment(sketch, "E630", {"start": v(-32.01, 6.39) * mm, "end": v(-31.87, 6.4) * mm});
            skLineSegment(sketch, "E631", {"start": v(-31.87, 6.4) * mm, "end": v(-31.74, 6.43) * mm});
            skLineSegment(sketch, "E632", {"start": v(-31.74, 6.43) * mm, "end": v(-31.62, 6.46) * mm});
            skLineSegment(sketch, "E633", {"start": v(-31.62, 6.46) * mm, "end": v(-31.5, 6.5) * mm});
            skLineSegment(sketch, "E634", {"start": v(-31.5, 6.5) * mm, "end": v(-31.4, 6.56) * mm});
            skLineSegment(sketch, "E635", {"start": v(-31.4, 6.56) * mm, "end": v(-31.29, 6.62) * mm});
            skLineSegment(sketch, "E636", {"start": v(-31.29, 6.62) * mm, "end": v(-31.19, 6.7) * mm});
            skLineSegment(sketch, "E637", {"start": v(-31.19, 6.7) * mm, "end": v(-31.1, 6.78) * mm});
            skLineSegment(sketch, "E638", {"start": v(-31.1, 6.78) * mm, "end": v(-31.01, 6.87) * mm});
            skLineSegment(sketch, "E639", {"start": v(-31.01, 6.87) * mm, "end": v(-30.94, 6.97) * mm});
            skLineSegment(sketch, "E640", {"start": v(-30.94, 6.97) * mm, "end": v(-30.88, 7.07) * mm});
            skLineSegment(sketch, "E641", {"start": v(-30.88, 7.07) * mm, "end": v(-30.84, 7.18) * mm});
            skLineSegment(sketch, "E642", {"start": v(-30.84, 7.18) * mm, "end": v(-30.8, 7.3) * mm});
            skLineSegment(sketch, "E643", {"start": v(-30.8, 7.3) * mm, "end": v(-30.78, 7.4) * mm});
            skLineSegment(sketch, "E644", {"start": v(-30.78, 7.4) * mm, "end": v(-30.77, 7.53) * mm});
            skLineSegment(sketch, "E645", {"start": v(-30.77, 7.53) * mm, "end": v(-30.77, 7.66) * mm});
            skLineSegment(sketch, "E646", {"start": v(-30.77, 7.66) * mm, "end": v(-30.78, 7.8) * mm});
            skLineSegment(sketch, "E647", {"start": v(-30.78, 7.8) * mm, "end": v(-30.8, 7.91) * mm});
            skLineSegment(sketch, "E648", {"start": v(-30.8, 7.91) * mm, "end": v(-30.84, 8.03) * mm});
            skLineSegment(sketch, "E649", {"start": v(-30.84, 8.03) * mm, "end": v(-30.88, 8.14) * mm});
            skLineSegment(sketch, "E650", {"start": v(-30.88, 8.14) * mm, "end": v(-30.94, 8.24) * mm});
            skLineSegment(sketch, "E651", {"start": v(-30.94, 8.24) * mm, "end": v(-31, 8.34) * mm});
            skLineSegment(sketch, "E652", {"start": v(-31, 8.34) * mm, "end": v(-31.09, 8.43) * mm});
            skLineSegment(sketch, "E653", {"start": v(-31.09, 8.43) * mm, "end": v(-31.18, 8.51) * mm});
            skLineSegment(sketch, "E654", {"start": v(-31.18, 8.51) * mm, "end": v(-31.28, 8.59) * mm});
            skLineSegment(sketch, "E655", {"start": v(-31.28, 8.59) * mm, "end": v(-31.39, 8.65) * mm});
            skLineSegment(sketch, "E656", {"start": v(-31.39, 8.65) * mm, "end": v(-31.5, 8.7) * mm});
            skLineSegment(sketch, "E657", {"start": v(-31.5, 8.7) * mm, "end": v(-31.62, 8.75) * mm});
            skLineSegment(sketch, "E658", {"start": v(-31.62, 8.75) * mm, "end": v(-31.75, 8.78) * mm});
            skLineSegment(sketch, "E659", {"start": v(-31.75, 8.78) * mm, "end": v(-31.89, 8.8) * mm});
            skLineSegment(sketch, "E660", {"start": v(-31.89, 8.8) * mm, "end": v(-32.03, 8.82) * mm});
            skLineSegment(sketch, "E661", {"start": v(-32.03, 8.82) * mm, "end": v(-32.18, 8.82) * mm});
            skLineSegment(sketch, "E662", {"start": v(-32.18, 8.82) * mm, "end": v(-32.32, 8.81) * mm});
            skLineSegment(sketch, "E663", {"start": v(-32.32, 8.81) * mm, "end": v(-32.46, 8.8) * mm});
            skLineSegment(sketch, "E664", {"start": v(-32.46, 8.8) * mm, "end": v(-32.6, 8.77) * mm});
            skLineSegment(sketch, "E665", {"start": v(-32.6, 8.77) * mm, "end": v(-32.72, 8.73) * mm});
            skLineSegment(sketch, "E666", {"start": v(-32.72, 8.73) * mm, "end": v(-32.83, 8.68) * mm});
            skLineSegment(sketch, "E667", {"start": v(-32.83, 8.68) * mm, "end": v(-32.94, 8.63) * mm});
            skLineSegment(sketch, "E668", {"start": v(-32.94, 8.63) * mm, "end": v(-33.04, 8.56) * mm});
            skLineSegment(sketch, "E669", {"start": v(-33.04, 8.56) * mm, "end": v(-33.13, 8.48) * mm});
            skLineSegment(sketch, "E670", {"start": v(-33.13, 8.48) * mm, "end": v(-33.22, 8.4) * mm});
            skLineSegment(sketch, "E671", {"start": v(-33.22, 8.4) * mm, "end": v(-33.3, 8.3) * mm});
            skLineSegment(sketch, "E672", {"start": v(-33.3, 8.3) * mm, "end": v(-33.35, 8.2) * mm});
            skLineSegment(sketch, "E673", {"start": v(-33.35, 8.2) * mm, "end": v(-33.4, 8.1) * mm});
            skLineSegment(sketch, "E674", {"start": v(-33.4, 8.1) * mm, "end": v(-33.45, 7.99) * mm});
            skLineSegment(sketch, "E675", {"start": v(-33.45, 7.99) * mm, "end": v(-33.48, 7.87) * mm});
            skLineSegment(sketch, "E676", {"start": v(-33.48, 7.87) * mm, "end": v(-33.5, 7.74) * mm});
            skLineSegment(sketch, "E677", {"start": v(-33.5, 7.74) * mm, "end": v(-33.5, 7.6) * mm});
            skLineSegment(sketch, "E678", {"start": v(-34.33, 13.8) * mm, "end": v(-34.33, 13.83) * mm});
            skLineSegment(sketch, "E679", {"start": v(-34.33, 13.83) * mm, "end": v(-34.33, 13.9) * mm});
            skLineSegment(sketch, "E680", {"start": v(-34.33, 13.9) * mm, "end": v(-34.33, 13.97) * mm});
            skLineSegment(sketch, "E681", {"start": v(-34.33, 13.97) * mm, "end": v(-34.33, 14.05) * mm});
            skLineSegment(sketch, "E682", {"start": v(-34.33, 14.05) * mm, "end": v(-34.33, 14.1) * mm});
            skLineSegment(sketch, "E683", {"start": v(-34.33, 14.1) * mm, "end": v(-34.33, 14.15) * mm});
            skLineSegment(sketch, "E684", {"start": v(-34.33, 14.15) * mm, "end": v(-34.3, 14.23) * mm});
            skLineSegment(sketch, "E685", {"start": v(-34.3, 14.23) * mm, "end": v(-34.26, 14.3) * mm});
            skLineSegment(sketch, "E686", {"start": v(-34.26, 14.3) * mm, "end": v(-34.2, 14.36) * mm});
            skLineSegment(sketch, "E687", {"start": v(-34.2, 14.36) * mm, "end": v(-34.12, 14.4) * mm});
            skLineSegment(sketch, "E688", {"start": v(-34.12, 14.4) * mm, "end": v(-34.03, 14.41) * mm});
            skLineSegment(sketch, "E689", {"start": v(-34.03, 14.41) * mm, "end": v(-33.76, 14.41) * mm});
            skLineSegment(sketch, "E690", {"start": v(-33.76, 14.41) * mm, "end": v(-33.01, 14.41) * mm});
            skLineSegment(sketch, "E691", {"start": v(-33.01, 14.41) * mm, "end": v(-32.03, 14.41) * mm});
            skLineSegment(sketch, "E692", {"start": v(-32.03, 14.41) * mm, "end": v(-31.07, 14.41) * mm});
            skLineSegment(sketch, "E693", {"start": v(-31.07, 14.41) * mm, "end": v(-30.41, 14.41) * mm});
            skLineSegment(sketch, "E694", {"start": v(-30.41, 14.41) * mm, "end": v(-30.23, 14.41) * mm});
            skLineSegment(sketch, "E695", {"start": v(-30.23, 14.41) * mm, "end": v(-30.15, 14.4) * mm});
            skLineSegment(sketch, "E696", {"start": v(-30.15, 14.4) * mm, "end": v(-30.07, 14.35) * mm});
            skLineSegment(sketch, "E697", {"start": v(-30.07, 14.35) * mm, "end": v(-30.01, 14.29) * mm});
            skLineSegment(sketch, "E698", {"start": v(-30.01, 14.29) * mm, "end": v(-29.97, 14.21) * mm});
            skLineSegment(sketch, "E699", {"start": v(-29.97, 14.21) * mm, "end": v(-29.95, 14.13) * mm});
            skLineSegment(sketch, "E700", {"start": v(-29.95, 14.13) * mm, "end": v(-29.95, 14.08) * mm});
            skLineSegment(sketch, "E701", {"start": v(-29.95, 14.08) * mm, "end": v(-29.95, 14) * mm});
            skLineSegment(sketch, "E702", {"start": v(-29.95, 14) * mm, "end": v(-29.95, 13.88) * mm});
            skLineSegment(sketch, "E703", {"start": v(-29.95, 13.88) * mm, "end": v(-29.95, 13.76) * mm});
            skLineSegment(sketch, "E704", {"start": v(-29.95, 13.76) * mm, "end": v(-29.95, 13.68) * mm});
            skLineSegment(sketch, "E705", {"start": v(-29.95, 13.68) * mm, "end": v(-29.95, 13.64) * mm});
            skLineSegment(sketch, "E706", {"start": v(-29.95, 13.64) * mm, "end": v(-29.96, 13.6) * mm});
            skLineSegment(sketch, "E707", {"start": v(-29.96, 13.6) * mm, "end": v(-29.98, 13.54) * mm});
            skLineSegment(sketch, "E708", {"start": v(-29.98, 13.54) * mm, "end": v(-30, 13.5) * mm});
            skLineSegment(sketch, "E709", {"start": v(-30, 13.5) * mm, "end": v(-30.03, 13.45) * mm});
            skLineSegment(sketch, "E710", {"start": v(-30.03, 13.45) * mm, "end": v(-30.07, 13.41) * mm});
            skLineSegment(sketch, "E711", {"start": v(-30.07, 13.41) * mm, "end": v(-30.2, 13.33) * mm});
            skLineSegment(sketch, "E712", {"start": v(-30.2, 13.33) * mm, "end": v(-30.67, 13) * mm});
            skLineSegment(sketch, "E713", {"start": v(-30.67, 13) * mm, "end": v(-31.35, 12.5) * mm});
            skLineSegment(sketch, "E714", {"start": v(-31.35, 12.5) * mm, "end": v(-32.06, 12) * mm});
            skLineSegment(sketch, "E715", {"start": v(-32.06, 12) * mm, "end": v(-32.6, 11.63) * mm});
            skLineSegment(sketch, "E716", {"start": v(-32.6, 11.63) * mm, "end": v(-32.78, 11.5) * mm});
            skLineSegment(sketch, "E717", {"start": v(-32.78, 11.5) * mm, "end": v(-32.52, 11.5) * mm});
            skLineSegment(sketch, "E718", {"start": v(-32.52, 11.5) * mm, "end": v(-31.97, 11.5) * mm});
            skLineSegment(sketch, "E719", {"start": v(-31.97, 11.5) * mm, "end": v(-31.3, 11.5) * mm});
            skLineSegment(sketch, "E720", {"start": v(-31.3, 11.5) * mm, "end": v(-30.69, 11.5) * mm});
            skLineSegment(sketch, "E721", {"start": v(-30.69, 11.5) * mm, "end": v(-30.3, 11.5) * mm});
            skLineSegment(sketch, "E722", {"start": v(-30.3, 11.5) * mm, "end": v(-30.21, 11.5) * mm});
            skLineSegment(sketch, "E723", {"start": v(-30.21, 11.5) * mm, "end": v(-30.13, 11.47) * mm});
            skLineSegment(sketch, "E724", {"start": v(-30.13, 11.47) * mm, "end": v(-30.06, 11.42) * mm});
            skLineSegment(sketch, "E725", {"start": v(-30.06, 11.42) * mm, "end": v(-30, 11.35) * mm});
            skLineSegment(sketch, "E726", {"start": v(-30, 11.35) * mm, "end": v(-29.97, 11.27) * mm});
            skLineSegment(sketch, "E727", {"start": v(-29.97, 11.27) * mm, "end": v(-29.95, 11.19) * mm});
            skLineSegment(sketch, "E728", {"start": v(-29.95, 11.19) * mm, "end": v(-29.95, 11.16) * mm});
            skLineSegment(sketch, "E729", {"start": v(-29.95, 11.16) * mm, "end": v(-29.95, 11.1) * mm});
            skLineSegment(sketch, "E730", {"start": v(-29.95, 11.1) * mm, "end": v(-29.95, 11) * mm});
            skLineSegment(sketch, "E731", {"start": v(-29.95, 11) * mm, "end": v(-29.95, 10.92) * mm});
            skLineSegment(sketch, "E732", {"start": v(-29.95, 10.92) * mm, "end": v(-29.95, 10.87) * mm});
            skLineSegment(sketch, "E733", {"start": v(-29.95, 10.87) * mm, "end": v(-29.96, 10.82) * mm});
            skLineSegment(sketch, "E734", {"start": v(-29.96, 10.82) * mm, "end": v(-29.98, 10.74) * mm});
            skLineSegment(sketch, "E735", {"start": v(-29.98, 10.74) * mm, "end": v(-30.02, 10.66) * mm});
            skLineSegment(sketch, "E736", {"start": v(-30.02, 10.66) * mm, "end": v(-30.09, 10.6) * mm});
            skLineSegment(sketch, "E737", {"start": v(-30.09, 10.6) * mm, "end": v(-30.16, 10.57) * mm});
            skLineSegment(sketch, "E738", {"start": v(-30.16, 10.57) * mm, "end": v(-30.25, 10.55) * mm});
            skLineSegment(sketch, "E739", {"start": v(-30.25, 10.55) * mm, "end": v(-30.52, 10.55) * mm});
            skLineSegment(sketch, "E740", {"start": v(-30.52, 10.55) * mm, "end": v(-31.27, 10.55) * mm});
            skLineSegment(sketch, "E741", {"start": v(-31.27, 10.55) * mm, "end": v(-32.25, 10.55) * mm});
            skLineSegment(sketch, "E742", {"start": v(-32.25, 10.55) * mm, "end": v(-33.2, 10.55) * mm});
            skLineSegment(sketch, "E743", {"start": v(-33.2, 10.55) * mm, "end": v(-33.87, 10.55) * mm});
            skLineSegment(sketch, "E744", {"start": v(-33.87, 10.55) * mm, "end": v(-34.05, 10.55) * mm});
            skLineSegment(sketch, "E745", {"start": v(-34.05, 10.55) * mm, "end": v(-34.14, 10.57) * mm});
            skLineSegment(sketch, "E746", {"start": v(-34.14, 10.57) * mm, "end": v(-34.21, 10.62) * mm});
            skLineSegment(sketch, "E747", {"start": v(-34.21, 10.62) * mm, "end": v(-34.27, 10.68) * mm});
            skLineSegment(sketch, "E748", {"start": v(-34.27, 10.68) * mm, "end": v(-34.31, 10.75) * mm});
            skLineSegment(sketch, "E749", {"start": v(-34.31, 10.75) * mm, "end": v(-34.33, 10.84) * mm});
            skLineSegment(sketch, "E750", {"start": v(-34.33, 10.84) * mm, "end": v(-34.33, 10.89) * mm});
            skLineSegment(sketch, "E751", {"start": v(-34.33, 10.89) * mm, "end": v(-34.33, 10.97) * mm});
            skLineSegment(sketch, "E752", {"start": v(-34.33, 10.97) * mm, "end": v(-34.33, 11.1) * mm});
            skLineSegment(sketch, "E753", {"start": v(-34.33, 11.1) * mm, "end": v(-34.33, 11.21) * mm});
            skLineSegment(sketch, "E754", {"start": v(-34.33, 11.21) * mm, "end": v(-34.33, 11.3) * mm});
            skLineSegment(sketch, "E755", {"start": v(-34.33, 11.3) * mm, "end": v(-34.33, 11.34) * mm});
            skLineSegment(sketch, "E756", {"start": v(-34.33, 11.34) * mm, "end": v(-34.32, 11.4) * mm});
            skLineSegment(sketch, "E757", {"start": v(-34.32, 11.4) * mm, "end": v(-34.3, 11.44) * mm});
            skLineSegment(sketch, "E758", {"start": v(-34.3, 11.44) * mm, "end": v(-34.28, 11.49) * mm});
            skLineSegment(sketch, "E759", {"start": v(-34.28, 11.49) * mm, "end": v(-34.25, 11.53) * mm});
            skLineSegment(sketch, "E760", {"start": v(-34.25, 11.53) * mm, "end": v(-34.21, 11.57) * mm});
            skLineSegment(sketch, "E761", {"start": v(-34.21, 11.57) * mm, "end": v(-34.1, 11.65) * mm});
            skLineSegment(sketch, "E762", {"start": v(-34.1, 11.65) * mm, "end": v(-33.62, 12) * mm});
            skLineSegment(sketch, "E763", {"start": v(-33.62, 12) * mm, "end": v(-32.94, 12.48) * mm});
            skLineSegment(sketch, "E764", {"start": v(-32.94, 12.48) * mm, "end": v(-32.24, 12.98) * mm});
            skLineSegment(sketch, "E765", {"start": v(-32.24, 12.98) * mm, "end": v(-31.7, 13.36) * mm});
            skLineSegment(sketch, "E766", {"start": v(-31.7, 13.36) * mm, "end": v(-31.52, 13.5) * mm});
            skLineSegment(sketch, "E767", {"start": v(-31.52, 13.5) * mm, "end": v(-31.78, 13.5) * mm});
            skLineSegment(sketch, "E768", {"start": v(-31.78, 13.5) * mm, "end": v(-32.33, 13.5) * mm});
            skLineSegment(sketch, "E769", {"start": v(-32.33, 13.5) * mm, "end": v(-33, 13.5) * mm});
            skLineSegment(sketch, "E770", {"start": v(-33, 13.5) * mm, "end": v(-33.6, 13.5) * mm});
            skLineSegment(sketch, "E771", {"start": v(-33.6, 13.5) * mm, "end": v(-33.97, 13.5) * mm});
            skLineSegment(sketch, "E772", {"start": v(-33.97, 13.5) * mm, "end": v(-34.07, 13.5) * mm});
            skLineSegment(sketch, "E773", {"start": v(-34.07, 13.5) * mm, "end": v(-34.15, 13.52) * mm});
            skLineSegment(sketch, "E774", {"start": v(-34.15, 13.52) * mm, "end": v(-34.22, 13.57) * mm});
            skLineSegment(sketch, "E775", {"start": v(-34.22, 13.57) * mm, "end": v(-34.28, 13.63) * mm});
            skLineSegment(sketch, "E776", {"start": v(-34.28, 13.63) * mm, "end": v(-34.32, 13.71) * mm});
            skLineSegment(sketch, "E777", {"start": v(-34.32, 13.71) * mm, "end": v(-34.33, 13.8) * mm});
            skSolve(sketch);
        }
        {
            var Q0;
            Q0=makeQuery(id+"F13.imprint","IMPRINT",FACE,{"disambiguationData":[TD([[makeQuery(id+"F13.imprint","IMPRINT",EDGE,{"derivedFrom":sQuery(id+"F13.wireOp",EDGE,"E678")}),-1.0]])]});
            var Q1;
            Q1=makeQuery(id+"F13.imprint","IMPRINT",FACE,{"disambiguationData":[TD([[makeQuery(id+"F13.imprint","IMPRINT",EDGE,{"derivedFrom":sQuery(id+"F13.wireOp",EDGE,"E548")}),-1.0]])]});
            var Q2;
            Q2=makeQuery(id+"F13.imprint","IMPRINT",FACE,{"disambiguationData":[TD([[makeQuery(id+"F13.imprint","IMPRINT",EDGE,{"derivedFrom":sQuery(id+"F13.wireOp",EDGE,"E405")}),-1.0]])]});
            var Q3;
            Q3=makeQuery(id+"F13.imprint","IMPRINT",FACE,{"disambiguationData":[TD([[makeQuery(id+"F13.imprint","IMPRINT",EDGE,{"derivedFrom":sQuery(id+"F13.wireOp",EDGE,"E306")}),-1.0]])]});
            var Q4;
            Q4=makeQuery(id+"F13.imprint","IMPRINT",FACE,{"disambiguationData":[TD([[makeQuery(id+"F13.imprint","IMPRINT",EDGE,{"derivedFrom":sQuery(id+"F13.wireOp",EDGE,"E206")}),-1.0]])]});
            var Q5;
            Q5=makeQuery(id+"F13.imprint","IMPRINT",FACE,{"disambiguationData":[TD([[makeQuery(id+"F13.imprint","IMPRINT",EDGE,{"derivedFrom":sQuery(id+"F13.wireOp",EDGE,"E106")}),-1.0]])]});
            var Q6;
            Q6=makeQuery(id+"F13.imprint","IMPRINT",FACE,{"disambiguationData":[TD([[makeQuery(id+"F13.imprint","IMPRINT",EDGE,{"derivedFrom":sQuery(id+"F13.wireOp",EDGE,"E6")}),-1.0]])]});
            extrude(context, id + "F14", {"entities" : qUnion([Q0, Q1, Q2, Q3, Q4, Q5, Q6]), "operationType" : NewBodyOperationType.REMOVE, "oppositeDirection" : true, "depth" : 1 * mm});
        }
    });
